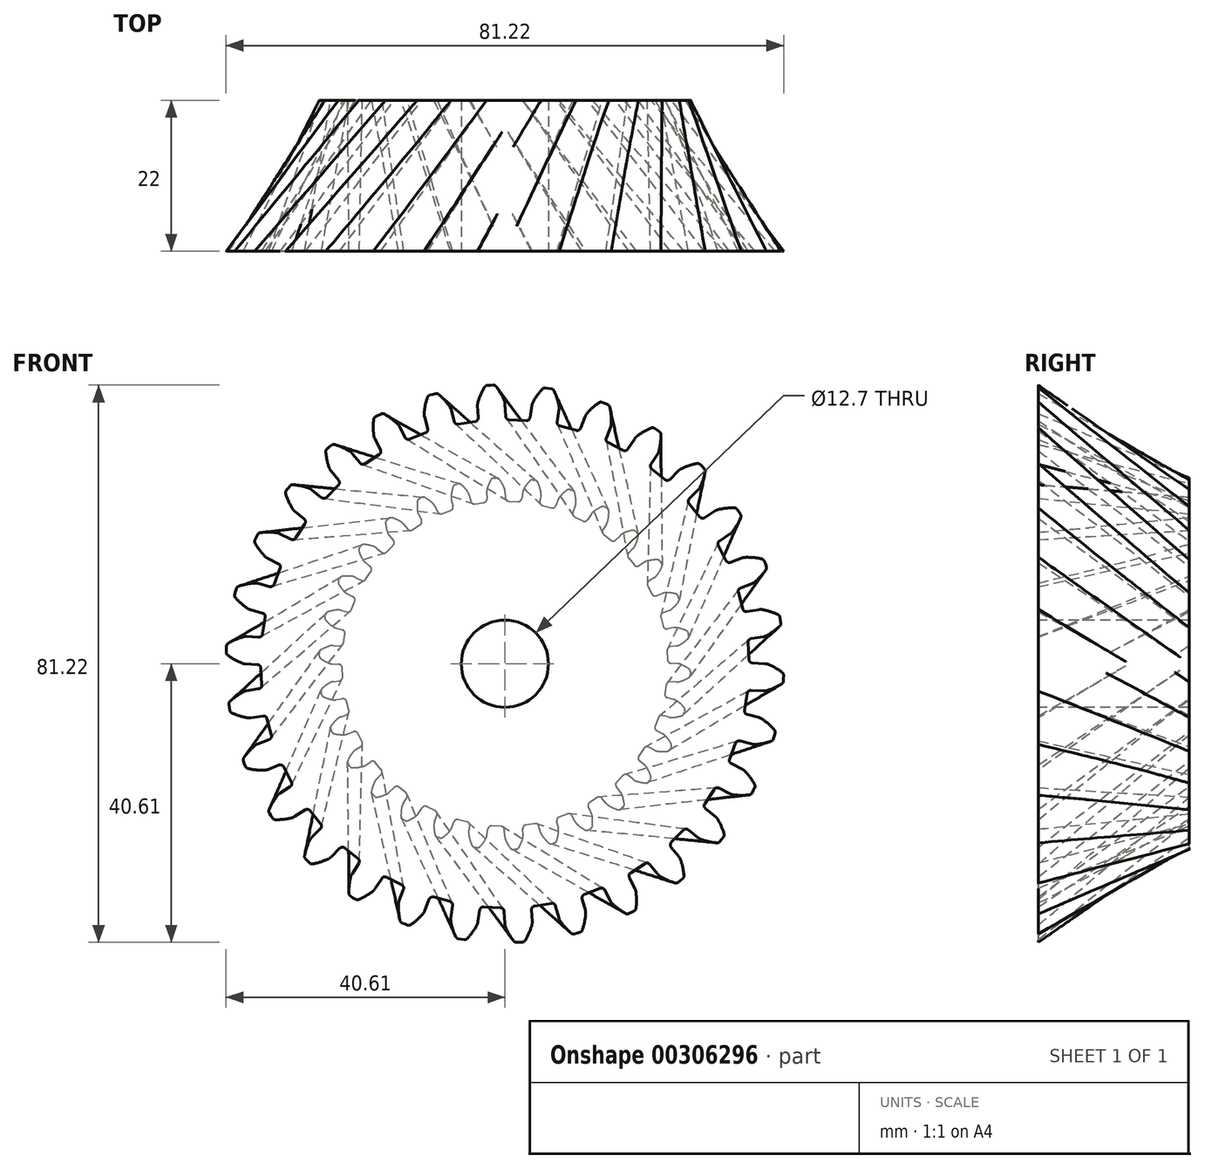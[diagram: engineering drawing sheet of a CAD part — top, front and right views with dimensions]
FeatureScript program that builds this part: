
annotation { "Feature Type Name" : "Feature", "Feature Type Description" : "" }
export const myFeature = defineFeature(function(context is Context, id is Id, definition is map)
    precondition{}
    {
        {
            var Q0;
            Q0=qCreatedBy(makeId("Front.planeOp"),FACE);
            var sketch = newSketch(context, id + "F0", { "sketchPlane" : qUnion([Q0])});
            skArc(sketch, "E0.trimOffspring", {"start": v(-0.11, 25.69) * mm, "mid": v(-0.42, 26.29) * mm, "end": v(-0.78, 26.85) * mm});
            skLineSegment(sketch, "E1", {"start": v(-1.22, 27.06) * mm, "end": v(-1.42, 27.05) * mm});
            skLineSegment(sketch, "E2.MirrorCS", {"start": v(-1.61, 27.04) * mm, "end": v(-1.42, 27.05) * mm});
            skArc(sketch, "E3.MirrorCS", {"start": v(-2.57, 25.56) * mm, "mid": v(-2.33, 26.19) * mm, "end": v(-2.03, 26.79) * mm});
            skLineSegment(sketch, "E4", {"start": v(0.02, 25.13) * mm, "end": v(0.07, 24.2) * mm});
            skLineSegment(sketch, "E5.MirrorCS", {"start": v(-2.65, 25) * mm, "end": v(-2.6, 24.06) * mm});
            skPoint(sketch, "E6.orphan", {"position": v(-2.54, 23.04) * mm});
            skPoint(sketch, "E7.orphan", {"position": v(0.12, 23.18) * mm});
            skPoint(sketch, "E8.visualSharp", {"position": v(-2.66, 25.26) * mm});
            skArc(sketch, "E8.filletArc", {"start": v(-2.57, 25.56) * mm, "mid": v(-2.64, 25.28) * mm, "end": v(-2.65, 25) * mm});
            skPoint(sketch, "E9.visualSharp", {"position": v(0, 25.4) * mm});
            skArc(sketch, "E9.filletArc", {"start": v(0.02, 25.13) * mm, "mid": v(-0.02, 25.42) * mm, "end": v(-0.11, 25.69) * mm});
            skPoint(sketch, "E10.visualSharp", {"position": v(-1.88, 27.03) * mm});
            skArc(sketch, "E10.filletArc", {"start": v(-1.61, 27.04) * mm, "mid": v(-1.85, 26.97) * mm, "end": v(-2.03, 26.79) * mm});
            skPoint(sketch, "E11.visualSharp", {"position": v(-0.95, 27.08) * mm});
            skArc(sketch, "E11.filletArc", {"start": v(-0.78, 26.85) * mm, "mid": v(-0.98, 27.01) * mm, "end": v(-1.22, 27.06) * mm});
            skPoint(sketch, "E12.visualSharp", {"position": v(-2.57, 23.57) * mm});
            skArc(sketch, "E12.filletArc", {"start": v(-3.06, 23.5) * mm, "mid": v(-2.72, 23.7) * mm, "end": v(-2.6, 24.06) * mm});
            skPoint(sketch, "E13.visualSharp", {"position": v(0.1, 23.7) * mm});
            skArc(sketch, "E13.filletArc", {"start": v(0.07, 24.2) * mm, "mid": v(0.23, 23.85) * mm, "end": v(0.59, 23.7) * mm});
            skLineSegment(sketch, "E14.1.0", {"start": v(-5.2, 24.58) * mm, "end": v(-4.97, 23.69) * mm});
            skPoint(sketch, "E14.1.1", {"position": v(-7.46, 26.05) * mm});
            skPoint(sketch, "E14.1.2", {"position": v(-6.56, 26.29) * mm});
            skPoint(sketch, "E14.1.3", {"position": v(-4.84, 23.2) * mm});
            skLineSegment(sketch, "E14.1.4", {"start": v(-7.78, 23.9) * mm, "end": v(-7.54, 23) * mm});
            skArc(sketch, "E14.1.5", {"start": v(-7.83, 24.47) * mm, "mid": v(-7.73, 25.13) * mm, "end": v(-7.55, 25.78) * mm});
            skPoint(sketch, "E14.1.6", {"position": v(-7.85, 24.16) * mm});
            skPoint(sketch, "E14.1.7", {"position": v(-7.42, 22.52) * mm});
            skArc(sketch, "E14.1.8", {"start": v(-5.45, 25.1) * mm, "mid": v(-5.87, 25.63) * mm, "end": v(-6.35, 26.1) * mm});
            skPoint(sketch, "E14.1.9", {"position": v(-5.28, 24.85) * mm});
            skPoint(sketch, "E14.1.10", {"position": v(-4.7, 22.7) * mm});
            skArc(sketch, "E14.1.11", {"start": v(-4.97, 23.69) * mm, "mid": v(-4.73, 23.38) * mm, "end": v(-4.35, 23.3) * mm});
            skArc(sketch, "E14.1.12", {"start": v(-7.83, 24.47) * mm, "mid": v(-7.83, 24.18) * mm, "end": v(-7.78, 23.9) * mm});
            skArc(sketch, "E14.1.13", {"start": v(-5.2, 24.58) * mm, "mid": v(-5.3, 24.86) * mm, "end": v(-5.45, 25.1) * mm});
            skArc(sketch, "E14.1.14", {"start": v(-7.88, 22.36) * mm, "mid": v(-7.59, 22.61) * mm, "end": v(-7.54, 23) * mm});
            skLineSegment(sketch, "E14.1.15", {"start": v(-6.82, 26.22) * mm, "end": v(-7.01, 26.17) * mm});
            skArc(sketch, "E14.1.16", {"start": v(-6.35, 26.1) * mm, "mid": v(-6.57, 26.22) * mm, "end": v(-6.82, 26.22) * mm});
            skLineSegment(sketch, "E14.1.17", {"start": v(-7.2, 26.12) * mm, "end": v(-7.01, 26.17) * mm});
            skArc(sketch, "E14.1.18", {"start": v(-7.2, 26.12) * mm, "mid": v(-7.42, 26) * mm, "end": v(-7.55, 25.78) * mm});
            skLineSegment(sketch, "E14.2.0", {"start": v(-10.2, 22.97) * mm, "end": v(-9.78, 22.14) * mm});
            skPoint(sketch, "E14.2.1", {"position": v(-12.71, 23.93) * mm});
            skPoint(sketch, "E14.2.2", {"position": v(-11.88, 24.35) * mm});
            skPoint(sketch, "E14.2.3", {"position": v(-9.56, 21.7) * mm});
            skLineSegment(sketch, "E14.2.4", {"start": v(-12.58, 21.75) * mm, "end": v(-12.16, 20.93) * mm});
            skArc(sketch, "E14.2.5", {"start": v(-12.75, 22.3) * mm, "mid": v(-12.78, 22.98) * mm, "end": v(-12.75, 23.65) * mm});
            skPoint(sketch, "E14.2.6", {"position": v(-12.7, 22) * mm});
            skPoint(sketch, "E14.2.7", {"position": v(-11.94, 20.48) * mm});
            skArc(sketch, "E14.2.8", {"start": v(-10.55, 23.42) * mm, "mid": v(-11.07, 23.85) * mm, "end": v(-11.64, 24.21) * mm});
            skPoint(sketch, "E14.2.9", {"position": v(-10.33, 23.2) * mm});
            skPoint(sketch, "E14.2.10", {"position": v(-9.32, 21.23) * mm});
            skArc(sketch, "E14.2.11", {"start": v(-9.78, 22.14) * mm, "mid": v(-9.5, 21.88) * mm, "end": v(-9.1, 21.89) * mm});
            skArc(sketch, "E14.2.12", {"start": v(-12.75, 22.3) * mm, "mid": v(-12.69, 22.02) * mm, "end": v(-12.58, 21.75) * mm});
            skArc(sketch, "E14.2.13", {"start": v(-10.2, 22.97) * mm, "mid": v(-10.36, 23.2) * mm, "end": v(-10.55, 23.42) * mm});
            skArc(sketch, "E14.2.14", {"start": v(-12.36, 20.23) * mm, "mid": v(-12.12, 20.54) * mm, "end": v(-12.16, 20.93) * mm});
            skLineSegment(sketch, "E14.2.15", {"start": v(-12.12, 24.23) * mm, "end": v(-12.3, 24.14) * mm});
            skArc(sketch, "E14.2.16", {"start": v(-11.64, 24.21) * mm, "mid": v(-11.88, 24.28) * mm, "end": v(-12.12, 24.23) * mm});
            skLineSegment(sketch, "E14.2.17", {"start": v(-12.47, 24.05) * mm, "end": v(-12.3, 24.14) * mm});
            skArc(sketch, "E14.2.18", {"start": v(-12.47, 24.05) * mm, "mid": v(-12.66, 23.88) * mm, "end": v(-12.75, 23.65) * mm});
            skPoint(sketch, "E14.center", {"position": v(0, 0) * mm});
            skPoint(sketch, "E15.3.3.0", {"position": v(-17.4, 20.76) * mm});
            skPoint(sketch, "E15.4.3.0", {"position": v(-16.69, 21.35) * mm});
            skPoint(sketch, "E15.5.3.0", {"position": v(-13.86, 19.23) * mm});
            skLineSegment(sketch, "E15.6.3.0", {"start": v(-16.83, 18.66) * mm, "end": v(-16.25, 17.94) * mm});
            skArc(sketch, "E15.9.3.0", {"start": v(-17.1, 19.17) * mm, "mid": v(-17.28, 19.82) * mm, "end": v(-17.39, 20.48) * mm});
            skPoint(sketch, "E15.13.3.0", {"position": v(-17, 18.87) * mm});
            skPoint(sketch, "E15.14.3.0", {"position": v(-15.93, 17.55) * mm});
            skArc(sketch, "E15.15.3.0", {"start": v(-15.2, 20.72) * mm, "mid": v(-15.8, 21.02) * mm, "end": v(-16.42, 21.26) * mm});
            skLineSegment(sketch, "E15.16.3.0", {"start": v(-14.75, 20.34) * mm, "end": v(-14.17, 19.62) * mm});
            skPoint(sketch, "E15.19.3.0", {"position": v(-14.93, 20.55) * mm});
            skPoint(sketch, "E15.20.3.0", {"position": v(-13.53, 18.82) * mm});
            skArc(sketch, "E15.21.3.0", {"start": v(-14.17, 19.62) * mm, "mid": v(-13.83, 19.43) * mm, "end": v(-13.45, 19.52) * mm});
            skArc(sketch, "E15.25.3.0", {"start": v(-17.1, 19.17) * mm, "mid": v(-17, 18.9) * mm, "end": v(-16.83, 18.66) * mm});
            skArc(sketch, "E15.29.3.0", {"start": v(-14.75, 20.34) * mm, "mid": v(-14.96, 20.55) * mm, "end": v(-15.2, 20.72) * mm});
            skArc(sketch, "E15.33.3.0", {"start": v(-16.3, 17.22) * mm, "mid": v(-16.13, 17.57) * mm, "end": v(-16.25, 17.94) * mm});
            skLineSegment(sketch, "E15.37.3.0", {"start": v(-16.9, 21.18) * mm, "end": v(-17.05, 21.05) * mm});
            skArc(sketch, "E15.40.3.0", {"start": v(-16.42, 21.26) * mm, "mid": v(-16.67, 21.28) * mm, "end": v(-16.9, 21.18) * mm});
            skLineSegment(sketch, "E15.44.3.0", {"start": v(-17.2, 20.93) * mm, "end": v(-17.05, 21.05) * mm});
            skArc(sketch, "E15.47.3.0", {"start": v(-17.2, 20.93) * mm, "mid": v(-17.35, 20.73) * mm, "end": v(-17.39, 20.48) * mm});
            skPoint(sketch, "E15.3.4.0", {"position": v(-21.35, 16.69) * mm});
            skPoint(sketch, "E15.4.4.0", {"position": v(-20.76, 17.4) * mm});
            skPoint(sketch, "E15.5.4.0", {"position": v(-17.55, 15.93) * mm});
            skLineSegment(sketch, "E15.6.4.0", {"start": v(-20.34, 14.75) * mm, "end": v(-19.62, 14.17) * mm});
            skArc(sketch, "E15.9.4.0", {"start": v(-20.72, 15.2) * mm, "mid": v(-21.02, 15.8) * mm, "end": v(-21.26, 16.42) * mm});
            skPoint(sketch, "E15.13.4.0", {"position": v(-20.55, 14.93) * mm});
            skPoint(sketch, "E15.14.4.0", {"position": v(-19.23, 13.86) * mm});
            skArc(sketch, "E15.15.4.0", {"start": v(-19.17, 17.1) * mm, "mid": v(-19.82, 17.28) * mm, "end": v(-20.48, 17.39) * mm});
            skLineSegment(sketch, "E15.16.4.0", {"start": v(-18.66, 16.83) * mm, "end": v(-17.94, 16.25) * mm});
            skPoint(sketch, "E15.19.4.0", {"position": v(-18.87, 17) * mm});
            skPoint(sketch, "E15.20.4.0", {"position": v(-17.14, 15.6) * mm});
            skArc(sketch, "E15.21.4.0", {"start": v(-17.94, 16.25) * mm, "mid": v(-17.57, 16.13) * mm, "end": v(-17.22, 16.3) * mm});
            skArc(sketch, "E15.25.4.0", {"start": v(-20.72, 15.2) * mm, "mid": v(-20.55, 14.96) * mm, "end": v(-20.34, 14.75) * mm});
            skArc(sketch, "E15.29.4.0", {"start": v(-18.66, 16.83) * mm, "mid": v(-18.9, 17) * mm, "end": v(-19.17, 17.1) * mm});
            skArc(sketch, "E15.33.4.0", {"start": v(-19.52, 13.45) * mm, "mid": v(-19.43, 13.83) * mm, "end": v(-19.62, 14.17) * mm});
            skLineSegment(sketch, "E15.37.4.0", {"start": v(-20.93, 17.2) * mm, "end": v(-21.05, 17.05) * mm});
            skArc(sketch, "E15.40.4.0", {"start": v(-20.48, 17.39) * mm, "mid": v(-20.73, 17.35) * mm, "end": v(-20.93, 17.2) * mm});
            skLineSegment(sketch, "E15.44.4.0", {"start": v(-21.18, 16.9) * mm, "end": v(-21.05, 17.05) * mm});
            skArc(sketch, "E15.47.4.0", {"start": v(-21.18, 16.9) * mm, "mid": v(-21.28, 16.67) * mm, "end": v(-21.26, 16.42) * mm});
            skPoint(sketch, "E15.3.5.0", {"position": v(-24.35, 11.88) * mm});
            skPoint(sketch, "E15.4.5.0", {"position": v(-23.93, 12.71) * mm});
            skPoint(sketch, "E15.5.5.0", {"position": v(-20.48, 11.94) * mm});
            skLineSegment(sketch, "E15.6.5.0", {"start": v(-22.97, 10.2) * mm, "end": v(-22.14, 9.78) * mm});
            skArc(sketch, "E15.9.5.0", {"start": v(-23.42, 10.55) * mm, "mid": v(-23.85, 11.07) * mm, "end": v(-24.21, 11.64) * mm});
            skPoint(sketch, "E15.13.5.0", {"position": v(-23.2, 10.33) * mm});
            skPoint(sketch, "E15.14.5.0", {"position": v(-21.7, 9.56) * mm});
            skArc(sketch, "E15.15.5.0", {"start": v(-22.3, 12.75) * mm, "mid": v(-22.98, 12.78) * mm, "end": v(-23.65, 12.75) * mm});
            skLineSegment(sketch, "E15.16.5.0", {"start": v(-21.75, 12.58) * mm, "end": v(-20.93, 12.16) * mm});
            skPoint(sketch, "E15.19.5.0", {"position": v(-22, 12.7) * mm});
            skPoint(sketch, "E15.20.5.0", {"position": v(-20.01, 11.7) * mm});
            skArc(sketch, "E15.21.5.0", {"start": v(-20.93, 12.16) * mm, "mid": v(-20.54, 12.12) * mm, "end": v(-20.23, 12.36) * mm});
            skArc(sketch, "E15.25.5.0", {"start": v(-23.42, 10.55) * mm, "mid": v(-23.2, 10.36) * mm, "end": v(-22.97, 10.2) * mm});
            skArc(sketch, "E15.29.5.0", {"start": v(-21.75, 12.58) * mm, "mid": v(-22.02, 12.69) * mm, "end": v(-22.3, 12.75) * mm});
            skArc(sketch, "E15.33.5.0", {"start": v(-21.89, 9.1) * mm, "mid": v(-21.88, 9.5) * mm, "end": v(-22.14, 9.78) * mm});
            skLineSegment(sketch, "E15.37.5.0", {"start": v(-24.05, 12.47) * mm, "end": v(-24.14, 12.3) * mm});
            skArc(sketch, "E15.40.5.0", {"start": v(-23.65, 12.75) * mm, "mid": v(-23.88, 12.66) * mm, "end": v(-24.05, 12.47) * mm});
            skLineSegment(sketch, "E15.44.5.0", {"start": v(-24.23, 12.12) * mm, "end": v(-24.14, 12.3) * mm});
            skArc(sketch, "E15.47.5.0", {"start": v(-24.23, 12.12) * mm, "mid": v(-24.28, 11.88) * mm, "end": v(-24.21, 11.64) * mm});
            skPoint(sketch, "E15.3.6.0", {"position": v(-26.29, 6.56) * mm});
            skPoint(sketch, "E15.4.6.0", {"position": v(-26.05, 7.46) * mm});
            skPoint(sketch, "E15.5.6.0", {"position": v(-22.52, 7.42) * mm});
            skLineSegment(sketch, "E15.6.6.0", {"start": v(-24.58, 5.2) * mm, "end": v(-23.69, 4.97) * mm});
            skArc(sketch, "E15.9.6.0", {"start": v(-25.1, 5.45) * mm, "mid": v(-25.63, 5.87) * mm, "end": v(-26.1, 6.35) * mm});
            skPoint(sketch, "E15.13.6.0", {"position": v(-24.85, 5.28) * mm});
            skPoint(sketch, "E15.14.6.0", {"position": v(-23.2, 4.84) * mm});
            skArc(sketch, "E15.15.6.0", {"start": v(-24.47, 7.83) * mm, "mid": v(-25.13, 7.73) * mm, "end": v(-25.78, 7.55) * mm});
            skLineSegment(sketch, "E15.16.6.0", {"start": v(-23.9, 7.78) * mm, "end": v(-23, 7.54) * mm});
            skPoint(sketch, "E15.19.6.0", {"position": v(-24.16, 7.85) * mm});
            skPoint(sketch, "E15.20.6.0", {"position": v(-22, 7.28) * mm});
            skArc(sketch, "E15.21.6.0", {"start": v(-23, 7.54) * mm, "mid": v(-22.61, 7.59) * mm, "end": v(-22.36, 7.88) * mm});
            skArc(sketch, "E15.25.6.0", {"start": v(-25.1, 5.45) * mm, "mid": v(-24.86, 5.3) * mm, "end": v(-24.58, 5.2) * mm});
            skArc(sketch, "E15.29.6.0", {"start": v(-23.9, 7.78) * mm, "mid": v(-24.18, 7.83) * mm, "end": v(-24.47, 7.83) * mm});
            skArc(sketch, "E15.33.6.0", {"start": v(-23.3, 4.35) * mm, "mid": v(-23.38, 4.73) * mm, "end": v(-23.69, 4.97) * mm});
            skLineSegment(sketch, "E15.37.6.0", {"start": v(-26.12, 7.2) * mm, "end": v(-26.17, 7.01) * mm});
            skArc(sketch, "E15.40.6.0", {"start": v(-25.78, 7.55) * mm, "mid": v(-26, 7.42) * mm, "end": v(-26.12, 7.2) * mm});
            skLineSegment(sketch, "E15.44.6.0", {"start": v(-26.22, 6.82) * mm, "end": v(-26.17, 7.01) * mm});
            skArc(sketch, "E15.47.6.0", {"start": v(-26.22, 6.82) * mm, "mid": v(-26.22, 6.57) * mm, "end": v(-26.1, 6.35) * mm});
            skPoint(sketch, "E15.3.7.0", {"position": v(-27.08, 0.95) * mm});
            skPoint(sketch, "E15.4.7.0", {"position": v(-27.03, 1.88) * mm});
            skPoint(sketch, "E15.5.7.0", {"position": v(-23.57, 2.57) * mm});
            skLineSegment(sketch, "E15.6.7.0", {"start": v(-25.13, -0.02) * mm, "end": v(-24.2, -0.07) * mm});
            skArc(sketch, "E15.9.7.0", {"start": v(-25.69, 0.11) * mm, "mid": v(-26.29, 0.42) * mm, "end": v(-26.85, 0.78) * mm});
            skPoint(sketch, "E15.13.7.0", {"position": v(-25.4, 0) * mm});
            skPoint(sketch, "E15.14.7.0", {"position": v(-23.7, -0.1) * mm});
            skArc(sketch, "E15.15.7.0", {"start": v(-25.56, 2.57) * mm, "mid": v(-26.19, 2.33) * mm, "end": v(-26.79, 2.03) * mm});
            skLineSegment(sketch, "E15.16.7.0", {"start": v(-25, 2.65) * mm, "end": v(-24.06, 2.6) * mm});
            skPoint(sketch, "E15.19.7.0", {"position": v(-25.26, 2.66) * mm});
            skPoint(sketch, "E15.20.7.0", {"position": v(-23.04, 2.54) * mm});
            skArc(sketch, "E15.21.7.0", {"start": v(-24.06, 2.6) * mm, "mid": v(-23.7, 2.72) * mm, "end": v(-23.5, 3.06) * mm});
            skArc(sketch, "E15.25.7.0", {"start": v(-25.69, 0.11) * mm, "mid": v(-25.42, 0.02) * mm, "end": v(-25.13, -0.02) * mm});
            skArc(sketch, "E15.29.7.0", {"start": v(-25, 2.65) * mm, "mid": v(-25.28, 2.64) * mm, "end": v(-25.56, 2.57) * mm});
            skArc(sketch, "E15.33.7.0", {"start": v(-23.7, -0.59) * mm, "mid": v(-23.85, -0.23) * mm, "end": v(-24.2, -0.07) * mm});
            skLineSegment(sketch, "E15.37.7.0", {"start": v(-27.04, 1.61) * mm, "end": v(-27.05, 1.42) * mm});
            skArc(sketch, "E15.40.7.0", {"start": v(-26.79, 2.03) * mm, "mid": v(-26.97, 1.85) * mm, "end": v(-27.04, 1.61) * mm});
            skLineSegment(sketch, "E15.44.7.0", {"start": v(-27.06, 1.22) * mm, "end": v(-27.05, 1.42) * mm});
            skArc(sketch, "E15.47.7.0", {"start": v(-27.06, 1.22) * mm, "mid": v(-27.01, 0.98) * mm, "end": v(-26.85, 0.78) * mm});
            skPoint(sketch, "E15.3.8.0", {"position": v(-26.68, -4.7) * mm});
            skPoint(sketch, "E15.4.8.0", {"position": v(-26.83, -3.78) * mm});
            skPoint(sketch, "E15.5.8.0", {"position": v(-23.59, -2.38) * mm});
            skLineSegment(sketch, "E15.6.8.0", {"start": v(-24.58, -5.24) * mm, "end": v(-23.66, -5.1) * mm});
            skArc(sketch, "E15.9.8.0", {"start": v(-25.15, -5.23) * mm, "mid": v(-25.8, -5.06) * mm, "end": v(-26.43, -4.82) * mm});
            skPoint(sketch, "E15.13.8.0", {"position": v(-24.84, -5.29) * mm});
            skPoint(sketch, "E15.14.8.0", {"position": v(-23.17, -5.02) * mm});
            skArc(sketch, "E15.15.8.0", {"start": v(-25.54, -2.8) * mm, "mid": v(-26.1, -3.16) * mm, "end": v(-26.62, -3.59) * mm});
            skLineSegment(sketch, "E15.16.8.0", {"start": v(-25, -2.6) * mm, "end": v(-24.08, -2.46) * mm});
            skPoint(sketch, "E15.19.8.0", {"position": v(-25.26, -2.65) * mm});
            skPoint(sketch, "E15.20.8.0", {"position": v(-23.07, -2.3) * mm});
            skArc(sketch, "E15.21.8.0", {"start": v(-24.08, -2.46) * mm, "mid": v(-23.74, -2.27) * mm, "end": v(-23.63, -1.9) * mm});
            skArc(sketch, "E15.25.8.0", {"start": v(-25.15, -5.23) * mm, "mid": v(-24.86, -5.26) * mm, "end": v(-24.58, -5.24) * mm});
            skArc(sketch, "E15.29.8.0", {"start": v(-25, -2.6) * mm, "mid": v(-25.27, -2.68) * mm, "end": v(-25.54, -2.8) * mm});
            skArc(sketch, "E15.33.8.0", {"start": v(-23.06, -5.5) * mm, "mid": v(-23.28, -5.18) * mm, "end": v(-23.66, -5.1) * mm});
            skLineSegment(sketch, "E15.37.8.0", {"start": v(-26.79, -4.04) * mm, "end": v(-26.76, -4.24) * mm});
            skArc(sketch, "E15.40.8.0", {"start": v(-26.62, -3.59) * mm, "mid": v(-26.76, -3.8) * mm, "end": v(-26.79, -4.04) * mm});
            skLineSegment(sketch, "E15.44.8.0", {"start": v(-26.73, -4.43) * mm, "end": v(-26.76, -4.24) * mm});
            skArc(sketch, "E15.47.8.0", {"start": v(-26.73, -4.43) * mm, "mid": v(-26.63, -4.66) * mm, "end": v(-26.43, -4.82) * mm});
            skPoint(sketch, "E15.3.9.0", {"position": v(-25.12, -10.14) * mm});
            skPoint(sketch, "E15.4.9.0", {"position": v(-25.46, -9.27) * mm});
            skPoint(sketch, "E15.5.9.0", {"position": v(-22.58, -7.24) * mm});
            skLineSegment(sketch, "E15.6.9.0", {"start": v(-22.95, -10.24) * mm, "end": v(-22.08, -9.9) * mm});
            skArc(sketch, "E15.9.9.0", {"start": v(-23.51, -10.34) * mm, "mid": v(-24.19, -10.31) * mm, "end": v(-24.85, -10.2) * mm});
            skPoint(sketch, "E15.13.9.0", {"position": v(-23.2, -10.34) * mm});
            skPoint(sketch, "E15.14.9.0", {"position": v(-21.62, -9.73) * mm});
            skArc(sketch, "E15.15.9.0", {"start": v(-24.4, -8.05) * mm, "mid": v(-24.87, -8.52) * mm, "end": v(-25.3, -9.04) * mm});
            skLineSegment(sketch, "E15.16.9.0", {"start": v(-23.9, -7.75) * mm, "end": v(-23.04, -7.41) * mm});
            skPoint(sketch, "E15.19.9.0", {"position": v(-24.16, -7.84) * mm});
            skPoint(sketch, "E15.20.9.0", {"position": v(-22.08, -7.05) * mm});
            skArc(sketch, "E15.21.9.0", {"start": v(-23.04, -7.41) * mm, "mid": v(-22.75, -7.15) * mm, "end": v(-22.72, -6.76) * mm});
            skArc(sketch, "E15.25.9.0", {"start": v(-23.51, -10.34) * mm, "mid": v(-23.23, -10.32) * mm, "end": v(-22.95, -10.24) * mm});
            skArc(sketch, "E15.29.9.0", {"start": v(-23.9, -7.75) * mm, "mid": v(-24.16, -7.87) * mm, "end": v(-24.4, -8.05) * mm});
            skArc(sketch, "E15.33.9.0", {"start": v(-21.41, -10.18) * mm, "mid": v(-21.7, -9.91) * mm, "end": v(-22.08, -9.9) * mm});
            skLineSegment(sketch, "E15.37.9.0", {"start": v(-25.36, -9.52) * mm, "end": v(-25.3, -9.7) * mm});
            skArc(sketch, "E15.40.9.0", {"start": v(-25.3, -9.04) * mm, "mid": v(-25.39, -9.28) * mm, "end": v(-25.36, -9.52) * mm});
            skLineSegment(sketch, "E15.44.9.0", {"start": v(-25.22, -9.9) * mm, "end": v(-25.3, -9.7) * mm});
            skArc(sketch, "E15.47.9.0", {"start": v(-25.22, -9.9) * mm, "mid": v(-25.08, -10.1) * mm, "end": v(-24.85, -10.2) * mm});
            skPoint(sketch, "E15.3.10.0", {"position": v(-22.47, -15.14) * mm});
            skPoint(sketch, "E15.4.10.0", {"position": v(-22.97, -14.36) * mm});
            skPoint(sketch, "E15.5.10.0", {"position": v(-20.58, -11.77) * mm});
            skLineSegment(sketch, "E15.6.10.0", {"start": v(-20.32, -14.79) * mm, "end": v(-19.54, -14.28) * mm});
            skArc(sketch, "E15.9.10.0", {"start": v(-20.85, -15) * mm, "mid": v(-21.51, -15.11) * mm, "end": v(-22.19, -15.15) * mm});
            skPoint(sketch, "E15.13.10.0", {"position": v(-20.55, -14.93) * mm});
            skPoint(sketch, "E15.14.10.0", {"position": v(-19.12, -14.01) * mm});
            skArc(sketch, "E15.15.10.0", {"start": v(-22.2, -12.94) * mm, "mid": v(-22.56, -13.5) * mm, "end": v(-22.86, -14.1) * mm});
            skLineSegment(sketch, "E15.16.10.0", {"start": v(-21.77, -12.55) * mm, "end": v(-21, -12.04) * mm});
            skPoint(sketch, "E15.19.10.0", {"position": v(-22, -12.7) * mm});
            skPoint(sketch, "E15.20.10.0", {"position": v(-20.14, -11.48) * mm});
            skArc(sketch, "E15.21.10.0", {"start": v(-21, -12.04) * mm, "mid": v(-20.77, -11.73) * mm, "end": v(-20.82, -11.34) * mm});
            skArc(sketch, "E15.25.10.0", {"start": v(-20.85, -15) * mm, "mid": v(-20.57, -14.92) * mm, "end": v(-20.32, -14.79) * mm});
            skArc(sketch, "E15.29.10.0", {"start": v(-21.77, -12.55) * mm, "mid": v(-22, -12.73) * mm, "end": v(-22.2, -12.94) * mm});
            skArc(sketch, "E15.33.10.0", {"start": v(-18.83, -14.4) * mm, "mid": v(-19.16, -14.2) * mm, "end": v(-19.54, -14.28) * mm});
            skLineSegment(sketch, "E15.37.10.0", {"start": v(-22.83, -14.59) * mm, "end": v(-22.72, -14.75) * mm});
            skArc(sketch, "E15.40.10.0", {"start": v(-22.86, -14.1) * mm, "mid": v(-22.9, -14.35) * mm, "end": v(-22.83, -14.59) * mm});
            skLineSegment(sketch, "E15.44.10.0", {"start": v(-22.61, -14.92) * mm, "end": v(-22.72, -14.75) * mm});
            skArc(sketch, "E15.47.10.0", {"start": v(-22.61, -14.92) * mm, "mid": v(-22.43, -15.09) * mm, "end": v(-22.19, -15.15) * mm});
            skPoint(sketch, "E15.3.11.0", {"position": v(-18.83, -19.48) * mm});
            skPoint(sketch, "E15.4.11.0", {"position": v(-19.48, -18.83) * mm});
            skPoint(sketch, "E15.5.11.0", {"position": v(-17.68, -15.8) * mm});
            skLineSegment(sketch, "E15.6.11.0", {"start": v(-16.8, -18.69) * mm, "end": v(-16.15, -18.03) * mm});
            skArc(sketch, "E15.9.11.0", {"start": v(-17.27, -19.01) * mm, "mid": v(-17.9, -19.26) * mm, "end": v(-18.55, -19.43) * mm});
            skPoint(sketch, "E15.13.11.0", {"position": v(-17, -18.88) * mm});
            skPoint(sketch, "E15.14.11.0", {"position": v(-15.8, -17.68) * mm});
            skArc(sketch, "E15.15.11.0", {"start": v(-19.01, -17.27) * mm, "mid": v(-19.26, -17.9) * mm, "end": v(-19.43, -18.55) * mm});
            skLineSegment(sketch, "E15.16.11.0", {"start": v(-18.69, -16.8) * mm, "end": v(-18.03, -16.15) * mm});
            skPoint(sketch, "E15.19.11.0", {"position": v(-18.88, -17) * mm});
            skPoint(sketch, "E15.20.11.0", {"position": v(-17.3, -15.42) * mm});
            skArc(sketch, "E15.21.11.0", {"start": v(-18.03, -16.15) * mm, "mid": v(-17.88, -15.79) * mm, "end": v(-18, -15.42) * mm});
            skArc(sketch, "E15.25.11.0", {"start": v(-17.27, -19.01) * mm, "mid": v(-17.02, -18.87) * mm, "end": v(-16.8, -18.69) * mm});
            skArc(sketch, "E15.29.11.0", {"start": v(-18.69, -16.8) * mm, "mid": v(-18.87, -17.02) * mm, "end": v(-19.01, -17.27) * mm});
            skArc(sketch, "E15.33.11.0", {"start": v(-15.42, -18) * mm, "mid": v(-15.79, -17.88) * mm, "end": v(-16.15, -18.03) * mm});
            skLineSegment(sketch, "E15.37.11.0", {"start": v(-19.3, -19.02) * mm, "end": v(-19.16, -19.16) * mm});
            skArc(sketch, "E15.40.11.0", {"start": v(-19.43, -18.55) * mm, "mid": v(-19.42, -18.8) * mm, "end": v(-19.3, -19.02) * mm});
            skLineSegment(sketch, "E15.44.11.0", {"start": v(-19.02, -19.3) * mm, "end": v(-19.16, -19.16) * mm});
            skArc(sketch, "E15.47.11.0", {"start": v(-19.02, -19.3) * mm, "mid": v(-18.8, -19.42) * mm, "end": v(-18.55, -19.43) * mm});
            skPoint(sketch, "E15.3.12.0", {"position": v(-14.36, -22.97) * mm});
            skPoint(sketch, "E15.4.12.0", {"position": v(-15.14, -22.47) * mm});
            skPoint(sketch, "E15.5.12.0", {"position": v(-14.01, -19.12) * mm});
            skLineSegment(sketch, "E15.6.12.0", {"start": v(-12.55, -21.77) * mm, "end": v(-12.04, -21) * mm});
            skArc(sketch, "E15.9.12.0", {"start": v(-12.94, -22.2) * mm, "mid": v(-13.5, -22.56) * mm, "end": v(-14.1, -22.86) * mm});
            skPoint(sketch, "E15.13.12.0", {"position": v(-12.7, -22) * mm});
            skPoint(sketch, "E15.14.12.0", {"position": v(-11.77, -20.58) * mm});
            skArc(sketch, "E15.15.12.0", {"start": v(-15, -20.85) * mm, "mid": v(-15.11, -21.51) * mm, "end": v(-15.15, -22.19) * mm});
            skLineSegment(sketch, "E15.16.12.0", {"start": v(-14.79, -20.32) * mm, "end": v(-14.28, -19.54) * mm});
            skPoint(sketch, "E15.19.12.0", {"position": v(-14.93, -20.55) * mm});
            skPoint(sketch, "E15.20.12.0", {"position": v(-13.72, -18.68) * mm});
            skArc(sketch, "E15.21.12.0", {"start": v(-14.28, -19.54) * mm, "mid": v(-14.2, -19.16) * mm, "end": v(-14.4, -18.83) * mm});
            skArc(sketch, "E15.25.12.0", {"start": v(-12.94, -22.2) * mm, "mid": v(-12.73, -22) * mm, "end": v(-12.55, -21.77) * mm});
            skArc(sketch, "E15.29.12.0", {"start": v(-14.79, -20.32) * mm, "mid": v(-14.92, -20.57) * mm, "end": v(-15, -20.85) * mm});
            skArc(sketch, "E15.33.12.0", {"start": v(-11.34, -20.82) * mm, "mid": v(-11.73, -20.77) * mm, "end": v(-12.04, -21) * mm});
            skLineSegment(sketch, "E15.37.12.0", {"start": v(-14.92, -22.61) * mm, "end": v(-14.75, -22.72) * mm});
            skArc(sketch, "E15.40.12.0", {"start": v(-15.15, -22.19) * mm, "mid": v(-15.09, -22.43) * mm, "end": v(-14.92, -22.61) * mm});
            skLineSegment(sketch, "E15.44.12.0", {"start": v(-14.59, -22.83) * mm, "end": v(-14.75, -22.72) * mm});
            skArc(sketch, "E15.47.12.0", {"start": v(-14.59, -22.83) * mm, "mid": v(-14.35, -22.9) * mm, "end": v(-14.1, -22.86) * mm});
            skPoint(sketch, "E15.3.13.0", {"position": v(-9.27, -25.46) * mm});
            skPoint(sketch, "E15.4.13.0", {"position": v(-10.14, -25.12) * mm});
            skPoint(sketch, "E15.5.13.0", {"position": v(-9.73, -21.62) * mm});
            skLineSegment(sketch, "E15.6.13.0", {"start": v(-7.75, -23.9) * mm, "end": v(-7.41, -23.04) * mm});
            skArc(sketch, "E15.9.13.0", {"start": v(-8.05, -24.4) * mm, "mid": v(-8.52, -24.87) * mm, "end": v(-9.04, -25.3) * mm});
            skPoint(sketch, "E15.13.13.0", {"position": v(-7.84, -24.16) * mm});
            skPoint(sketch, "E15.14.13.0", {"position": v(-7.24, -22.58) * mm});
            skArc(sketch, "E15.15.13.0", {"start": v(-10.34, -23.51) * mm, "mid": v(-10.31, -24.19) * mm, "end": v(-10.2, -24.85) * mm});
            skLineSegment(sketch, "E15.16.13.0", {"start": v(-10.24, -22.95) * mm, "end": v(-9.9, -22.08) * mm});
            skPoint(sketch, "E15.19.13.0", {"position": v(-10.34, -23.2) * mm});
            skPoint(sketch, "E15.20.13.0", {"position": v(-9.54, -21.13) * mm});
            skArc(sketch, "E15.21.13.0", {"start": v(-9.9, -22.08) * mm, "mid": v(-9.91, -21.7) * mm, "end": v(-10.18, -21.41) * mm});
            skArc(sketch, "E15.25.13.0", {"start": v(-8.05, -24.4) * mm, "mid": v(-7.87, -24.16) * mm, "end": v(-7.75, -23.9) * mm});
            skArc(sketch, "E15.29.13.0", {"start": v(-10.24, -22.95) * mm, "mid": v(-10.32, -23.23) * mm, "end": v(-10.34, -23.51) * mm});
            skArc(sketch, "E15.33.13.0", {"start": v(-6.76, -22.72) * mm, "mid": v(-7.15, -22.75) * mm, "end": v(-7.41, -23.04) * mm});
            skLineSegment(sketch, "E15.37.13.0", {"start": v(-9.9, -25.22) * mm, "end": v(-9.7, -25.3) * mm});
            skArc(sketch, "E15.40.13.0", {"start": v(-10.2, -24.85) * mm, "mid": v(-10.1, -25.08) * mm, "end": v(-9.9, -25.22) * mm});
            skLineSegment(sketch, "E15.44.13.0", {"start": v(-9.52, -25.36) * mm, "end": v(-9.7, -25.3) * mm});
            skArc(sketch, "E15.47.13.0", {"start": v(-9.52, -25.36) * mm, "mid": v(-9.28, -25.39) * mm, "end": v(-9.04, -25.3) * mm});
            skPoint(sketch, "E15.3.14.0", {"position": v(-3.78, -26.83) * mm});
            skPoint(sketch, "E15.4.14.0", {"position": v(-4.7, -26.68) * mm});
            skPoint(sketch, "E15.5.14.0", {"position": v(-5.02, -23.17) * mm});
            skLineSegment(sketch, "E15.6.14.0", {"start": v(-2.6, -25) * mm, "end": v(-2.46, -24.08) * mm});
            skArc(sketch, "E15.9.14.0", {"start": v(-2.8, -25.54) * mm, "mid": v(-3.16, -26.1) * mm, "end": v(-3.59, -26.62) * mm});
            skPoint(sketch, "E15.13.14.0", {"position": v(-2.65, -25.26) * mm});
            skPoint(sketch, "E15.14.14.0", {"position": v(-2.38, -23.59) * mm});
            skArc(sketch, "E15.15.14.0", {"start": v(-5.23, -25.15) * mm, "mid": v(-5.06, -25.8) * mm, "end": v(-4.82, -26.43) * mm});
            skLineSegment(sketch, "E15.16.14.0", {"start": v(-5.24, -24.58) * mm, "end": v(-5.1, -23.66) * mm});
            skPoint(sketch, "E15.19.14.0", {"position": v(-5.29, -24.84) * mm});
            skPoint(sketch, "E15.20.14.0", {"position": v(-4.94, -22.65) * mm});
            skArc(sketch, "E15.21.14.0", {"start": v(-5.1, -23.66) * mm, "mid": v(-5.18, -23.28) * mm, "end": v(-5.5, -23.06) * mm});
            skArc(sketch, "E15.25.14.0", {"start": v(-2.8, -25.54) * mm, "mid": v(-2.68, -25.27) * mm, "end": v(-2.6, -25) * mm});
            skArc(sketch, "E15.29.14.0", {"start": v(-5.24, -24.58) * mm, "mid": v(-5.26, -24.86) * mm, "end": v(-5.23, -25.15) * mm});
            skArc(sketch, "E15.33.14.0", {"start": v(-1.9, -23.63) * mm, "mid": v(-2.27, -23.74) * mm, "end": v(-2.46, -24.08) * mm});
            skLineSegment(sketch, "E15.37.14.0", {"start": v(-4.43, -26.73) * mm, "end": v(-4.24, -26.76) * mm});
            skArc(sketch, "E15.40.14.0", {"start": v(-4.82, -26.43) * mm, "mid": v(-4.66, -26.63) * mm, "end": v(-4.43, -26.73) * mm});
            skLineSegment(sketch, "E15.44.14.0", {"start": v(-4.04, -26.79) * mm, "end": v(-4.24, -26.76) * mm});
            skArc(sketch, "E15.47.14.0", {"start": v(-4.04, -26.79) * mm, "mid": v(-3.8, -26.76) * mm, "end": v(-3.59, -26.62) * mm});
            skPoint(sketch, "E15.3.15.0", {"position": v(1.88, -27.03) * mm});
            skPoint(sketch, "E15.4.15.0", {"position": v(0.95, -27.08) * mm});
            skPoint(sketch, "E15.5.15.0", {"position": v(-0.1, -23.7) * mm});
            skLineSegment(sketch, "E15.6.15.0", {"start": v(2.65, -25) * mm, "end": v(2.6, -24.06) * mm});
            skArc(sketch, "E15.9.15.0", {"start": v(2.57, -25.56) * mm, "mid": v(2.33, -26.19) * mm, "end": v(2.03, -26.79) * mm});
            skPoint(sketch, "E15.13.15.0", {"position": v(2.66, -25.26) * mm});
            skPoint(sketch, "E15.14.15.0", {"position": v(2.57, -23.57) * mm});
            skArc(sketch, "E15.15.15.0", {"start": v(0.11, -25.69) * mm, "mid": v(0.42, -26.29) * mm, "end": v(0.78, -26.85) * mm});
            skLineSegment(sketch, "E15.16.15.0", {"start": v(-0.02, -25.13) * mm, "end": v(-0.07, -24.2) * mm});
            skPoint(sketch, "E15.19.15.0", {"position": v(0, -25.4) * mm});
            skPoint(sketch, "E15.20.15.0", {"position": v(-0.12, -23.18) * mm});
            skArc(sketch, "E15.21.15.0", {"start": v(-0.07, -24.2) * mm, "mid": v(-0.23, -23.85) * mm, "end": v(-0.59, -23.7) * mm});
            skArc(sketch, "E15.25.15.0", {"start": v(2.57, -25.56) * mm, "mid": v(2.64, -25.28) * mm, "end": v(2.65, -25) * mm});
            skArc(sketch, "E15.29.15.0", {"start": v(-0.02, -25.13) * mm, "mid": v(0.02, -25.42) * mm, "end": v(0.11, -25.69) * mm});
            skArc(sketch, "E15.33.15.0", {"start": v(3.06, -23.5) * mm, "mid": v(2.72, -23.7) * mm, "end": v(2.6, -24.06) * mm});
            skLineSegment(sketch, "E15.37.15.0", {"start": v(1.22, -27.06) * mm, "end": v(1.42, -27.05) * mm});
            skArc(sketch, "E15.40.15.0", {"start": v(0.78, -26.85) * mm, "mid": v(0.98, -27.01) * mm, "end": v(1.22, -27.06) * mm});
            skLineSegment(sketch, "E15.44.15.0", {"start": v(1.61, -27.04) * mm, "end": v(1.42, -27.05) * mm});
            skArc(sketch, "E15.47.15.0", {"start": v(1.61, -27.04) * mm, "mid": v(1.85, -26.97) * mm, "end": v(2.03, -26.79) * mm});
            skPoint(sketch, "E15.3.16.0", {"position": v(7.46, -26.05) * mm});
            skPoint(sketch, "E15.4.16.0", {"position": v(6.56, -26.29) * mm});
            skPoint(sketch, "E15.5.16.0", {"position": v(4.84, -23.2) * mm});
            skLineSegment(sketch, "E15.6.16.0", {"start": v(7.78, -23.9) * mm, "end": v(7.54, -23) * mm});
            skArc(sketch, "E15.9.16.0", {"start": v(7.83, -24.47) * mm, "mid": v(7.73, -25.13) * mm, "end": v(7.55, -25.78) * mm});
            skPoint(sketch, "E15.13.16.0", {"position": v(7.85, -24.16) * mm});
            skPoint(sketch, "E15.14.16.0", {"position": v(7.42, -22.52) * mm});
            skArc(sketch, "E15.15.16.0", {"start": v(5.45, -25.1) * mm, "mid": v(5.87, -25.63) * mm, "end": v(6.35, -26.1) * mm});
            skLineSegment(sketch, "E15.16.16.0", {"start": v(5.2, -24.58) * mm, "end": v(4.97, -23.69) * mm});
            skPoint(sketch, "E15.19.16.0", {"position": v(5.28, -24.85) * mm});
            skPoint(sketch, "E15.20.16.0", {"position": v(4.7, -22.7) * mm});
            skArc(sketch, "E15.21.16.0", {"start": v(4.97, -23.69) * mm, "mid": v(4.73, -23.38) * mm, "end": v(4.35, -23.3) * mm});
            skArc(sketch, "E15.25.16.0", {"start": v(7.83, -24.47) * mm, "mid": v(7.83, -24.18) * mm, "end": v(7.78, -23.9) * mm});
            skArc(sketch, "E15.29.16.0", {"start": v(5.2, -24.58) * mm, "mid": v(5.3, -24.86) * mm, "end": v(5.45, -25.1) * mm});
            skArc(sketch, "E15.33.16.0", {"start": v(7.88, -22.36) * mm, "mid": v(7.59, -22.61) * mm, "end": v(7.54, -23) * mm});
            skLineSegment(sketch, "E15.37.16.0", {"start": v(6.82, -26.22) * mm, "end": v(7.01, -26.17) * mm});
            skArc(sketch, "E15.40.16.0", {"start": v(6.35, -26.1) * mm, "mid": v(6.57, -26.22) * mm, "end": v(6.82, -26.22) * mm});
            skLineSegment(sketch, "E15.44.16.0", {"start": v(7.2, -26.12) * mm, "end": v(7.01, -26.17) * mm});
            skArc(sketch, "E15.47.16.0", {"start": v(7.2, -26.12) * mm, "mid": v(7.42, -26) * mm, "end": v(7.55, -25.78) * mm});
            skPoint(sketch, "E15.3.17.0", {"position": v(12.71, -23.93) * mm});
            skPoint(sketch, "E15.4.17.0", {"position": v(11.88, -24.35) * mm});
            skPoint(sketch, "E15.5.17.0", {"position": v(9.56, -21.7) * mm});
            skLineSegment(sketch, "E15.6.17.0", {"start": v(12.58, -21.75) * mm, "end": v(12.16, -20.93) * mm});
            skArc(sketch, "E15.9.17.0", {"start": v(12.75, -22.3) * mm, "mid": v(12.78, -22.98) * mm, "end": v(12.75, -23.65) * mm});
            skPoint(sketch, "E15.13.17.0", {"position": v(12.7, -22) * mm});
            skPoint(sketch, "E15.14.17.0", {"position": v(11.94, -20.48) * mm});
            skArc(sketch, "E15.15.17.0", {"start": v(10.55, -23.42) * mm, "mid": v(11.07, -23.85) * mm, "end": v(11.64, -24.21) * mm});
            skLineSegment(sketch, "E15.16.17.0", {"start": v(10.2, -22.97) * mm, "end": v(9.78, -22.14) * mm});
            skPoint(sketch, "E15.19.17.0", {"position": v(10.33, -23.2) * mm});
            skPoint(sketch, "E15.20.17.0", {"position": v(9.32, -21.23) * mm});
            skArc(sketch, "E15.21.17.0", {"start": v(9.78, -22.14) * mm, "mid": v(9.5, -21.88) * mm, "end": v(9.1, -21.89) * mm});
            skArc(sketch, "E15.25.17.0", {"start": v(12.75, -22.3) * mm, "mid": v(12.69, -22.02) * mm, "end": v(12.58, -21.75) * mm});
            skArc(sketch, "E15.29.17.0", {"start": v(10.2, -22.97) * mm, "mid": v(10.36, -23.2) * mm, "end": v(10.55, -23.42) * mm});
            skArc(sketch, "E15.33.17.0", {"start": v(12.36, -20.23) * mm, "mid": v(12.12, -20.54) * mm, "end": v(12.16, -20.93) * mm});
            skLineSegment(sketch, "E15.37.17.0", {"start": v(12.12, -24.23) * mm, "end": v(12.3, -24.14) * mm});
            skArc(sketch, "E15.40.17.0", {"start": v(11.64, -24.21) * mm, "mid": v(11.88, -24.28) * mm, "end": v(12.12, -24.23) * mm});
            skLineSegment(sketch, "E15.44.17.0", {"start": v(12.47, -24.05) * mm, "end": v(12.3, -24.14) * mm});
            skArc(sketch, "E15.47.17.0", {"start": v(12.47, -24.05) * mm, "mid": v(12.66, -23.88) * mm, "end": v(12.75, -23.65) * mm});
            skPoint(sketch, "E15.3.18.0", {"position": v(17.4, -20.76) * mm});
            skPoint(sketch, "E15.4.18.0", {"position": v(16.69, -21.35) * mm});
            skPoint(sketch, "E15.5.18.0", {"position": v(13.86, -19.23) * mm});
            skLineSegment(sketch, "E15.6.18.0", {"start": v(16.83, -18.66) * mm, "end": v(16.25, -17.94) * mm});
            skArc(sketch, "E15.9.18.0", {"start": v(17.1, -19.17) * mm, "mid": v(17.28, -19.82) * mm, "end": v(17.39, -20.48) * mm});
            skPoint(sketch, "E15.13.18.0", {"position": v(17, -18.87) * mm});
            skPoint(sketch, "E15.14.18.0", {"position": v(15.93, -17.55) * mm});
            skArc(sketch, "E15.15.18.0", {"start": v(15.2, -20.72) * mm, "mid": v(15.8, -21.02) * mm, "end": v(16.42, -21.26) * mm});
            skLineSegment(sketch, "E15.16.18.0", {"start": v(14.75, -20.34) * mm, "end": v(14.17, -19.62) * mm});
            skPoint(sketch, "E15.19.18.0", {"position": v(14.93, -20.55) * mm});
            skPoint(sketch, "E15.20.18.0", {"position": v(13.53, -18.82) * mm});
            skArc(sketch, "E15.21.18.0", {"start": v(14.17, -19.62) * mm, "mid": v(13.83, -19.43) * mm, "end": v(13.45, -19.52) * mm});
            skArc(sketch, "E15.25.18.0", {"start": v(17.1, -19.17) * mm, "mid": v(17, -18.9) * mm, "end": v(16.83, -18.66) * mm});
            skArc(sketch, "E15.29.18.0", {"start": v(14.75, -20.34) * mm, "mid": v(14.96, -20.55) * mm, "end": v(15.2, -20.72) * mm});
            skArc(sketch, "E15.33.18.0", {"start": v(16.3, -17.22) * mm, "mid": v(16.13, -17.57) * mm, "end": v(16.25, -17.94) * mm});
            skLineSegment(sketch, "E15.37.18.0", {"start": v(16.9, -21.18) * mm, "end": v(17.05, -21.05) * mm});
            skArc(sketch, "E15.40.18.0", {"start": v(16.42, -21.26) * mm, "mid": v(16.67, -21.28) * mm, "end": v(16.9, -21.18) * mm});
            skLineSegment(sketch, "E15.44.18.0", {"start": v(17.2, -20.93) * mm, "end": v(17.05, -21.05) * mm});
            skArc(sketch, "E15.47.18.0", {"start": v(17.2, -20.93) * mm, "mid": v(17.35, -20.73) * mm, "end": v(17.39, -20.48) * mm});
            skPoint(sketch, "E15.3.19.0", {"position": v(21.35, -16.69) * mm});
            skPoint(sketch, "E15.4.19.0", {"position": v(20.76, -17.4) * mm});
            skPoint(sketch, "E15.5.19.0", {"position": v(17.55, -15.93) * mm});
            skLineSegment(sketch, "E15.6.19.0", {"start": v(20.34, -14.75) * mm, "end": v(19.62, -14.17) * mm});
            skArc(sketch, "E15.9.19.0", {"start": v(20.72, -15.2) * mm, "mid": v(21.02, -15.8) * mm, "end": v(21.26, -16.42) * mm});
            skPoint(sketch, "E15.13.19.0", {"position": v(20.55, -14.93) * mm});
            skPoint(sketch, "E15.14.19.0", {"position": v(19.23, -13.86) * mm});
            skArc(sketch, "E15.15.19.0", {"start": v(19.17, -17.1) * mm, "mid": v(19.82, -17.28) * mm, "end": v(20.48, -17.39) * mm});
            skLineSegment(sketch, "E15.16.19.0", {"start": v(18.66, -16.83) * mm, "end": v(17.94, -16.25) * mm});
            skPoint(sketch, "E15.19.19.0", {"position": v(18.87, -17) * mm});
            skPoint(sketch, "E15.20.19.0", {"position": v(17.14, -15.6) * mm});
            skArc(sketch, "E15.21.19.0", {"start": v(17.94, -16.25) * mm, "mid": v(17.57, -16.13) * mm, "end": v(17.22, -16.3) * mm});
            skArc(sketch, "E15.25.19.0", {"start": v(20.72, -15.2) * mm, "mid": v(20.55, -14.96) * mm, "end": v(20.34, -14.75) * mm});
            skArc(sketch, "E15.29.19.0", {"start": v(18.66, -16.83) * mm, "mid": v(18.9, -17) * mm, "end": v(19.17, -17.1) * mm});
            skArc(sketch, "E15.33.19.0", {"start": v(19.52, -13.45) * mm, "mid": v(19.43, -13.83) * mm, "end": v(19.62, -14.17) * mm});
            skLineSegment(sketch, "E15.37.19.0", {"start": v(20.93, -17.2) * mm, "end": v(21.05, -17.05) * mm});
            skArc(sketch, "E15.40.19.0", {"start": v(20.48, -17.39) * mm, "mid": v(20.73, -17.35) * mm, "end": v(20.93, -17.2) * mm});
            skLineSegment(sketch, "E15.44.19.0", {"start": v(21.18, -16.9) * mm, "end": v(21.05, -17.05) * mm});
            skArc(sketch, "E15.47.19.0", {"start": v(21.18, -16.9) * mm, "mid": v(21.28, -16.67) * mm, "end": v(21.26, -16.42) * mm});
            skPoint(sketch, "E15.3.20.0", {"position": v(24.35, -11.88) * mm});
            skPoint(sketch, "E15.4.20.0", {"position": v(23.93, -12.71) * mm});
            skPoint(sketch, "E15.5.20.0", {"position": v(20.48, -11.94) * mm});
            skLineSegment(sketch, "E15.6.20.0", {"start": v(22.97, -10.2) * mm, "end": v(22.14, -9.78) * mm});
            skArc(sketch, "E15.9.20.0", {"start": v(23.42, -10.55) * mm, "mid": v(23.85, -11.07) * mm, "end": v(24.21, -11.64) * mm});
            skPoint(sketch, "E15.13.20.0", {"position": v(23.2, -10.33) * mm});
            skPoint(sketch, "E15.14.20.0", {"position": v(21.7, -9.56) * mm});
            skArc(sketch, "E15.15.20.0", {"start": v(22.3, -12.75) * mm, "mid": v(22.98, -12.78) * mm, "end": v(23.65, -12.75) * mm});
            skLineSegment(sketch, "E15.16.20.0", {"start": v(21.75, -12.58) * mm, "end": v(20.93, -12.16) * mm});
            skPoint(sketch, "E15.19.20.0", {"position": v(22, -12.7) * mm});
            skPoint(sketch, "E15.20.20.0", {"position": v(20.01, -11.7) * mm});
            skArc(sketch, "E15.21.20.0", {"start": v(20.93, -12.16) * mm, "mid": v(20.54, -12.12) * mm, "end": v(20.23, -12.36) * mm});
            skArc(sketch, "E15.25.20.0", {"start": v(23.42, -10.55) * mm, "mid": v(23.2, -10.36) * mm, "end": v(22.97, -10.2) * mm});
            skArc(sketch, "E15.29.20.0", {"start": v(21.75, -12.58) * mm, "mid": v(22.02, -12.69) * mm, "end": v(22.3, -12.75) * mm});
            skArc(sketch, "E15.33.20.0", {"start": v(21.89, -9.1) * mm, "mid": v(21.88, -9.5) * mm, "end": v(22.14, -9.78) * mm});
            skLineSegment(sketch, "E15.37.20.0", {"start": v(24.05, -12.47) * mm, "end": v(24.14, -12.3) * mm});
            skArc(sketch, "E15.40.20.0", {"start": v(23.65, -12.75) * mm, "mid": v(23.88, -12.66) * mm, "end": v(24.05, -12.47) * mm});
            skLineSegment(sketch, "E15.44.20.0", {"start": v(24.23, -12.12) * mm, "end": v(24.14, -12.3) * mm});
            skArc(sketch, "E15.47.20.0", {"start": v(24.23, -12.12) * mm, "mid": v(24.28, -11.88) * mm, "end": v(24.21, -11.64) * mm});
            skPoint(sketch, "E15.3.21.0", {"position": v(26.29, -6.56) * mm});
            skPoint(sketch, "E15.4.21.0", {"position": v(26.05, -7.46) * mm});
            skPoint(sketch, "E15.5.21.0", {"position": v(22.52, -7.42) * mm});
            skLineSegment(sketch, "E15.6.21.0", {"start": v(24.58, -5.2) * mm, "end": v(23.69, -4.97) * mm});
            skArc(sketch, "E15.9.21.0", {"start": v(25.1, -5.45) * mm, "mid": v(25.63, -5.87) * mm, "end": v(26.1, -6.35) * mm});
            skPoint(sketch, "E15.13.21.0", {"position": v(24.85, -5.28) * mm});
            skPoint(sketch, "E15.14.21.0", {"position": v(23.2, -4.84) * mm});
            skArc(sketch, "E15.15.21.0", {"start": v(24.47, -7.83) * mm, "mid": v(25.13, -7.73) * mm, "end": v(25.78, -7.55) * mm});
            skLineSegment(sketch, "E15.16.21.0", {"start": v(23.9, -7.78) * mm, "end": v(23, -7.54) * mm});
            skPoint(sketch, "E15.19.21.0", {"position": v(24.16, -7.85) * mm});
            skPoint(sketch, "E15.20.21.0", {"position": v(22, -7.28) * mm});
            skArc(sketch, "E15.21.21.0", {"start": v(23, -7.54) * mm, "mid": v(22.61, -7.59) * mm, "end": v(22.36, -7.88) * mm});
            skArc(sketch, "E15.25.21.0", {"start": v(25.1, -5.45) * mm, "mid": v(24.86, -5.3) * mm, "end": v(24.58, -5.2) * mm});
            skArc(sketch, "E15.29.21.0", {"start": v(23.9, -7.78) * mm, "mid": v(24.18, -7.83) * mm, "end": v(24.47, -7.83) * mm});
            skArc(sketch, "E15.33.21.0", {"start": v(23.3, -4.35) * mm, "mid": v(23.38, -4.73) * mm, "end": v(23.69, -4.97) * mm});
            skLineSegment(sketch, "E15.37.21.0", {"start": v(26.12, -7.2) * mm, "end": v(26.17, -7.01) * mm});
            skArc(sketch, "E15.40.21.0", {"start": v(25.78, -7.55) * mm, "mid": v(26, -7.42) * mm, "end": v(26.12, -7.2) * mm});
            skLineSegment(sketch, "E15.44.21.0", {"start": v(26.22, -6.82) * mm, "end": v(26.17, -7.01) * mm});
            skArc(sketch, "E15.47.21.0", {"start": v(26.22, -6.82) * mm, "mid": v(26.22, -6.57) * mm, "end": v(26.1, -6.35) * mm});
            skPoint(sketch, "E15.3.22.0", {"position": v(27.08, -0.95) * mm});
            skPoint(sketch, "E15.4.22.0", {"position": v(27.03, -1.88) * mm});
            skPoint(sketch, "E15.5.22.0", {"position": v(23.57, -2.57) * mm});
            skLineSegment(sketch, "E15.6.22.0", {"start": v(25.13, 0.02) * mm, "end": v(24.2, 0.07) * mm});
            skArc(sketch, "E15.9.22.0", {"start": v(25.69, -0.11) * mm, "mid": v(26.29, -0.42) * mm, "end": v(26.85, -0.78) * mm});
            skPoint(sketch, "E15.13.22.0", {"position": v(25.4, 0) * mm});
            skPoint(sketch, "E15.14.22.0", {"position": v(23.7, 0.1) * mm});
            skArc(sketch, "E15.15.22.0", {"start": v(25.56, -2.57) * mm, "mid": v(26.19, -2.33) * mm, "end": v(26.79, -2.03) * mm});
            skLineSegment(sketch, "E15.16.22.0", {"start": v(25, -2.65) * mm, "end": v(24.06, -2.6) * mm});
            skPoint(sketch, "E15.19.22.0", {"position": v(25.26, -2.66) * mm});
            skPoint(sketch, "E15.20.22.0", {"position": v(23.04, -2.54) * mm});
            skArc(sketch, "E15.21.22.0", {"start": v(24.06, -2.6) * mm, "mid": v(23.7, -2.72) * mm, "end": v(23.5, -3.06) * mm});
            skArc(sketch, "E15.25.22.0", {"start": v(25.69, -0.11) * mm, "mid": v(25.42, -0.02) * mm, "end": v(25.13, 0.02) * mm});
            skArc(sketch, "E15.29.22.0", {"start": v(25, -2.65) * mm, "mid": v(25.28, -2.64) * mm, "end": v(25.56, -2.57) * mm});
            skArc(sketch, "E15.33.22.0", {"start": v(23.7, 0.59) * mm, "mid": v(23.85, 0.23) * mm, "end": v(24.2, 0.07) * mm});
            skLineSegment(sketch, "E15.37.22.0", {"start": v(27.04, -1.61) * mm, "end": v(27.05, -1.42) * mm});
            skArc(sketch, "E15.40.22.0", {"start": v(26.79, -2.03) * mm, "mid": v(26.97, -1.85) * mm, "end": v(27.04, -1.61) * mm});
            skLineSegment(sketch, "E15.44.22.0", {"start": v(27.06, -1.22) * mm, "end": v(27.05, -1.42) * mm});
            skArc(sketch, "E15.47.22.0", {"start": v(27.06, -1.22) * mm, "mid": v(27.01, -0.98) * mm, "end": v(26.85, -0.78) * mm});
            skPoint(sketch, "E15.3.23.0", {"position": v(26.68, 4.7) * mm});
            skPoint(sketch, "E15.4.23.0", {"position": v(26.83, 3.78) * mm});
            skPoint(sketch, "E15.5.23.0", {"position": v(23.59, 2.38) * mm});
            skLineSegment(sketch, "E15.6.23.0", {"start": v(24.58, 5.24) * mm, "end": v(23.66, 5.1) * mm});
            skArc(sketch, "E15.9.23.0", {"start": v(25.15, 5.23) * mm, "mid": v(25.8, 5.06) * mm, "end": v(26.43, 4.82) * mm});
            skPoint(sketch, "E15.13.23.0", {"position": v(24.84, 5.29) * mm});
            skPoint(sketch, "E15.14.23.0", {"position": v(23.17, 5.02) * mm});
            skArc(sketch, "E15.15.23.0", {"start": v(25.54, 2.8) * mm, "mid": v(26.1, 3.16) * mm, "end": v(26.62, 3.59) * mm});
            skLineSegment(sketch, "E15.16.23.0", {"start": v(25, 2.6) * mm, "end": v(24.08, 2.46) * mm});
            skPoint(sketch, "E15.19.23.0", {"position": v(25.26, 2.65) * mm});
            skPoint(sketch, "E15.20.23.0", {"position": v(23.07, 2.3) * mm});
            skArc(sketch, "E15.21.23.0", {"start": v(24.08, 2.46) * mm, "mid": v(23.74, 2.27) * mm, "end": v(23.63, 1.9) * mm});
            skArc(sketch, "E15.25.23.0", {"start": v(25.15, 5.23) * mm, "mid": v(24.86, 5.26) * mm, "end": v(24.58, 5.24) * mm});
            skArc(sketch, "E15.29.23.0", {"start": v(25, 2.6) * mm, "mid": v(25.27, 2.68) * mm, "end": v(25.54, 2.8) * mm});
            skArc(sketch, "E15.33.23.0", {"start": v(23.06, 5.5) * mm, "mid": v(23.28, 5.18) * mm, "end": v(23.66, 5.1) * mm});
            skLineSegment(sketch, "E15.37.23.0", {"start": v(26.79, 4.04) * mm, "end": v(26.76, 4.24) * mm});
            skArc(sketch, "E15.40.23.0", {"start": v(26.62, 3.59) * mm, "mid": v(26.76, 3.8) * mm, "end": v(26.79, 4.04) * mm});
            skLineSegment(sketch, "E15.44.23.0", {"start": v(26.73, 4.43) * mm, "end": v(26.76, 4.24) * mm});
            skArc(sketch, "E15.47.23.0", {"start": v(26.73, 4.43) * mm, "mid": v(26.63, 4.66) * mm, "end": v(26.43, 4.82) * mm});
            skPoint(sketch, "E15.3.24.0", {"position": v(25.12, 10.14) * mm});
            skPoint(sketch, "E15.4.24.0", {"position": v(25.46, 9.27) * mm});
            skPoint(sketch, "E15.5.24.0", {"position": v(22.58, 7.24) * mm});
            skLineSegment(sketch, "E15.6.24.0", {"start": v(22.95, 10.24) * mm, "end": v(22.08, 9.9) * mm});
            skArc(sketch, "E15.9.24.0", {"start": v(23.51, 10.34) * mm, "mid": v(24.19, 10.31) * mm, "end": v(24.85, 10.2) * mm});
            skPoint(sketch, "E15.13.24.0", {"position": v(23.2, 10.34) * mm});
            skPoint(sketch, "E15.14.24.0", {"position": v(21.62, 9.73) * mm});
            skArc(sketch, "E15.15.24.0", {"start": v(24.4, 8.05) * mm, "mid": v(24.87, 8.52) * mm, "end": v(25.3, 9.04) * mm});
            skLineSegment(sketch, "E15.16.24.0", {"start": v(23.9, 7.75) * mm, "end": v(23.04, 7.41) * mm});
            skPoint(sketch, "E15.19.24.0", {"position": v(24.16, 7.84) * mm});
            skPoint(sketch, "E15.20.24.0", {"position": v(22.08, 7.05) * mm});
            skArc(sketch, "E15.21.24.0", {"start": v(23.04, 7.41) * mm, "mid": v(22.75, 7.15) * mm, "end": v(22.72, 6.76) * mm});
            skArc(sketch, "E15.25.24.0", {"start": v(23.51, 10.34) * mm, "mid": v(23.23, 10.32) * mm, "end": v(22.95, 10.24) * mm});
            skArc(sketch, "E15.29.24.0", {"start": v(23.9, 7.75) * mm, "mid": v(24.16, 7.87) * mm, "end": v(24.4, 8.05) * mm});
            skArc(sketch, "E15.33.24.0", {"start": v(21.41, 10.18) * mm, "mid": v(21.7, 9.91) * mm, "end": v(22.08, 9.9) * mm});
            skLineSegment(sketch, "E15.37.24.0", {"start": v(25.36, 9.52) * mm, "end": v(25.3, 9.7) * mm});
            skArc(sketch, "E15.40.24.0", {"start": v(25.3, 9.04) * mm, "mid": v(25.39, 9.28) * mm, "end": v(25.36, 9.52) * mm});
            skLineSegment(sketch, "E15.44.24.0", {"start": v(25.22, 9.9) * mm, "end": v(25.3, 9.7) * mm});
            skArc(sketch, "E15.47.24.0", {"start": v(25.22, 9.9) * mm, "mid": v(25.08, 10.1) * mm, "end": v(24.85, 10.2) * mm});
            skPoint(sketch, "E15.3.25.0", {"position": v(22.47, 15.14) * mm});
            skPoint(sketch, "E15.4.25.0", {"position": v(22.97, 14.36) * mm});
            skPoint(sketch, "E15.5.25.0", {"position": v(20.58, 11.77) * mm});
            skLineSegment(sketch, "E15.6.25.0", {"start": v(20.32, 14.79) * mm, "end": v(19.54, 14.28) * mm});
            skArc(sketch, "E15.9.25.0", {"start": v(20.85, 15) * mm, "mid": v(21.51, 15.11) * mm, "end": v(22.19, 15.15) * mm});
            skPoint(sketch, "E15.13.25.0", {"position": v(20.55, 14.93) * mm});
            skPoint(sketch, "E15.14.25.0", {"position": v(19.12, 14.01) * mm});
            skArc(sketch, "E15.15.25.0", {"start": v(22.2, 12.94) * mm, "mid": v(22.56, 13.5) * mm, "end": v(22.86, 14.1) * mm});
            skLineSegment(sketch, "E15.16.25.0", {"start": v(21.77, 12.55) * mm, "end": v(21, 12.04) * mm});
            skPoint(sketch, "E15.19.25.0", {"position": v(22, 12.7) * mm});
            skPoint(sketch, "E15.20.25.0", {"position": v(20.14, 11.48) * mm});
            skArc(sketch, "E15.21.25.0", {"start": v(21, 12.04) * mm, "mid": v(20.77, 11.73) * mm, "end": v(20.82, 11.34) * mm});
            skArc(sketch, "E15.25.25.0", {"start": v(20.85, 15) * mm, "mid": v(20.57, 14.92) * mm, "end": v(20.32, 14.79) * mm});
            skArc(sketch, "E15.29.25.0", {"start": v(21.77, 12.55) * mm, "mid": v(22, 12.73) * mm, "end": v(22.2, 12.94) * mm});
            skArc(sketch, "E15.33.25.0", {"start": v(18.83, 14.4) * mm, "mid": v(19.16, 14.2) * mm, "end": v(19.54, 14.28) * mm});
            skLineSegment(sketch, "E15.37.25.0", {"start": v(22.83, 14.59) * mm, "end": v(22.72, 14.75) * mm});
            skArc(sketch, "E15.40.25.0", {"start": v(22.86, 14.1) * mm, "mid": v(22.9, 14.35) * mm, "end": v(22.83, 14.59) * mm});
            skLineSegment(sketch, "E15.44.25.0", {"start": v(22.61, 14.92) * mm, "end": v(22.72, 14.75) * mm});
            skArc(sketch, "E15.47.25.0", {"start": v(22.61, 14.92) * mm, "mid": v(22.43, 15.09) * mm, "end": v(22.19, 15.15) * mm});
            skPoint(sketch, "E15.3.26.0", {"position": v(18.83, 19.48) * mm});
            skPoint(sketch, "E15.4.26.0", {"position": v(19.48, 18.83) * mm});
            skPoint(sketch, "E15.5.26.0", {"position": v(17.68, 15.8) * mm});
            skLineSegment(sketch, "E15.6.26.0", {"start": v(16.8, 18.69) * mm, "end": v(16.15, 18.03) * mm});
            skArc(sketch, "E15.9.26.0", {"start": v(17.27, 19.01) * mm, "mid": v(17.9, 19.26) * mm, "end": v(18.55, 19.43) * mm});
            skPoint(sketch, "E15.13.26.0", {"position": v(17, 18.88) * mm});
            skPoint(sketch, "E15.14.26.0", {"position": v(15.8, 17.68) * mm});
            skArc(sketch, "E15.15.26.0", {"start": v(19.01, 17.27) * mm, "mid": v(19.26, 17.9) * mm, "end": v(19.43, 18.55) * mm});
            skLineSegment(sketch, "E15.16.26.0", {"start": v(18.69, 16.8) * mm, "end": v(18.03, 16.15) * mm});
            skPoint(sketch, "E15.19.26.0", {"position": v(18.88, 17) * mm});
            skPoint(sketch, "E15.20.26.0", {"position": v(17.3, 15.42) * mm});
            skArc(sketch, "E15.21.26.0", {"start": v(18.03, 16.15) * mm, "mid": v(17.88, 15.79) * mm, "end": v(18, 15.42) * mm});
            skArc(sketch, "E15.25.26.0", {"start": v(17.27, 19.01) * mm, "mid": v(17.02, 18.87) * mm, "end": v(16.8, 18.69) * mm});
            skArc(sketch, "E15.29.26.0", {"start": v(18.69, 16.8) * mm, "mid": v(18.87, 17.02) * mm, "end": v(19.01, 17.27) * mm});
            skArc(sketch, "E15.33.26.0", {"start": v(15.42, 18) * mm, "mid": v(15.79, 17.88) * mm, "end": v(16.15, 18.03) * mm});
            skLineSegment(sketch, "E15.37.26.0", {"start": v(19.3, 19.02) * mm, "end": v(19.16, 19.16) * mm});
            skArc(sketch, "E15.40.26.0", {"start": v(19.43, 18.55) * mm, "mid": v(19.42, 18.8) * mm, "end": v(19.3, 19.02) * mm});
            skLineSegment(sketch, "E15.44.26.0", {"start": v(19.02, 19.3) * mm, "end": v(19.16, 19.16) * mm});
            skArc(sketch, "E15.47.26.0", {"start": v(19.02, 19.3) * mm, "mid": v(18.8, 19.42) * mm, "end": v(18.55, 19.43) * mm});
            skPoint(sketch, "E15.3.27.0", {"position": v(14.36, 22.97) * mm});
            skPoint(sketch, "E15.4.27.0", {"position": v(15.14, 22.47) * mm});
            skPoint(sketch, "E15.5.27.0", {"position": v(14.01, 19.12) * mm});
            skLineSegment(sketch, "E15.6.27.0", {"start": v(12.55, 21.77) * mm, "end": v(12.04, 21) * mm});
            skArc(sketch, "E15.9.27.0", {"start": v(12.94, 22.2) * mm, "mid": v(13.5, 22.56) * mm, "end": v(14.1, 22.86) * mm});
            skPoint(sketch, "E15.13.27.0", {"position": v(12.7, 22) * mm});
            skPoint(sketch, "E15.14.27.0", {"position": v(11.77, 20.58) * mm});
            skArc(sketch, "E15.15.27.0", {"start": v(15, 20.85) * mm, "mid": v(15.11, 21.51) * mm, "end": v(15.15, 22.19) * mm});
            skLineSegment(sketch, "E15.16.27.0", {"start": v(14.79, 20.32) * mm, "end": v(14.28, 19.54) * mm});
            skPoint(sketch, "E15.19.27.0", {"position": v(14.93, 20.55) * mm});
            skPoint(sketch, "E15.20.27.0", {"position": v(13.72, 18.68) * mm});
            skArc(sketch, "E15.21.27.0", {"start": v(14.28, 19.54) * mm, "mid": v(14.2, 19.16) * mm, "end": v(14.4, 18.83) * mm});
            skArc(sketch, "E15.25.27.0", {"start": v(12.94, 22.2) * mm, "mid": v(12.73, 22) * mm, "end": v(12.55, 21.77) * mm});
            skArc(sketch, "E15.29.27.0", {"start": v(14.79, 20.32) * mm, "mid": v(14.92, 20.57) * mm, "end": v(15, 20.85) * mm});
            skArc(sketch, "E15.33.27.0", {"start": v(11.34, 20.82) * mm, "mid": v(11.73, 20.77) * mm, "end": v(12.04, 21) * mm});
            skLineSegment(sketch, "E15.37.27.0", {"start": v(14.92, 22.61) * mm, "end": v(14.75, 22.72) * mm});
            skArc(sketch, "E15.40.27.0", {"start": v(15.15, 22.19) * mm, "mid": v(15.09, 22.43) * mm, "end": v(14.92, 22.61) * mm});
            skLineSegment(sketch, "E15.44.27.0", {"start": v(14.59, 22.83) * mm, "end": v(14.75, 22.72) * mm});
            skArc(sketch, "E15.47.27.0", {"start": v(14.59, 22.83) * mm, "mid": v(14.35, 22.9) * mm, "end": v(14.1, 22.86) * mm});
            skPoint(sketch, "E15.3.28.0", {"position": v(9.27, 25.46) * mm});
            skPoint(sketch, "E15.4.28.0", {"position": v(10.14, 25.12) * mm});
            skPoint(sketch, "E15.5.28.0", {"position": v(9.73, 21.62) * mm});
            skLineSegment(sketch, "E15.6.28.0", {"start": v(7.75, 23.9) * mm, "end": v(7.41, 23.04) * mm});
            skArc(sketch, "E15.9.28.0", {"start": v(8.05, 24.4) * mm, "mid": v(8.52, 24.87) * mm, "end": v(9.04, 25.3) * mm});
            skPoint(sketch, "E15.13.28.0", {"position": v(7.84, 24.16) * mm});
            skPoint(sketch, "E15.14.28.0", {"position": v(7.24, 22.58) * mm});
            skArc(sketch, "E15.15.28.0", {"start": v(10.34, 23.51) * mm, "mid": v(10.31, 24.19) * mm, "end": v(10.2, 24.85) * mm});
            skLineSegment(sketch, "E15.16.28.0", {"start": v(10.24, 22.95) * mm, "end": v(9.9, 22.08) * mm});
            skPoint(sketch, "E15.19.28.0", {"position": v(10.34, 23.2) * mm});
            skPoint(sketch, "E15.20.28.0", {"position": v(9.54, 21.13) * mm});
            skArc(sketch, "E15.21.28.0", {"start": v(9.9, 22.08) * mm, "mid": v(9.91, 21.7) * mm, "end": v(10.18, 21.41) * mm});
            skArc(sketch, "E15.25.28.0", {"start": v(8.05, 24.4) * mm, "mid": v(7.87, 24.16) * mm, "end": v(7.75, 23.9) * mm});
            skArc(sketch, "E15.29.28.0", {"start": v(10.24, 22.95) * mm, "mid": v(10.32, 23.23) * mm, "end": v(10.34, 23.51) * mm});
            skArc(sketch, "E15.33.28.0", {"start": v(6.76, 22.72) * mm, "mid": v(7.15, 22.75) * mm, "end": v(7.41, 23.04) * mm});
            skLineSegment(sketch, "E15.37.28.0", {"start": v(9.9, 25.22) * mm, "end": v(9.7, 25.3) * mm});
            skArc(sketch, "E15.40.28.0", {"start": v(10.2, 24.85) * mm, "mid": v(10.1, 25.08) * mm, "end": v(9.9, 25.22) * mm});
            skLineSegment(sketch, "E15.44.28.0", {"start": v(9.52, 25.36) * mm, "end": v(9.7, 25.3) * mm});
            skArc(sketch, "E15.47.28.0", {"start": v(9.52, 25.36) * mm, "mid": v(9.28, 25.39) * mm, "end": v(9.04, 25.3) * mm});
            skPoint(sketch, "E15.3.29.0", {"position": v(3.78, 26.83) * mm});
            skPoint(sketch, "E15.4.29.0", {"position": v(4.7, 26.68) * mm});
            skPoint(sketch, "E15.5.29.0", {"position": v(5.02, 23.17) * mm});
            skLineSegment(sketch, "E15.6.29.0", {"start": v(2.6, 25) * mm, "end": v(2.46, 24.08) * mm});
            skArc(sketch, "E15.9.29.0", {"start": v(2.8, 25.54) * mm, "mid": v(3.16, 26.1) * mm, "end": v(3.59, 26.62) * mm});
            skPoint(sketch, "E15.13.29.0", {"position": v(2.65, 25.26) * mm});
            skPoint(sketch, "E15.14.29.0", {"position": v(2.38, 23.59) * mm});
            skArc(sketch, "E15.15.29.0", {"start": v(5.23, 25.15) * mm, "mid": v(5.06, 25.8) * mm, "end": v(4.82, 26.43) * mm});
            skLineSegment(sketch, "E15.16.29.0", {"start": v(5.24, 24.58) * mm, "end": v(5.1, 23.66) * mm});
            skPoint(sketch, "E15.19.29.0", {"position": v(5.29, 24.84) * mm});
            skPoint(sketch, "E15.20.29.0", {"position": v(4.94, 22.65) * mm});
            skArc(sketch, "E15.21.29.0", {"start": v(5.1, 23.66) * mm, "mid": v(5.18, 23.28) * mm, "end": v(5.5, 23.06) * mm});
            skArc(sketch, "E15.25.29.0", {"start": v(2.8, 25.54) * mm, "mid": v(2.68, 25.27) * mm, "end": v(2.6, 25) * mm});
            skArc(sketch, "E15.29.29.0", {"start": v(5.24, 24.58) * mm, "mid": v(5.26, 24.86) * mm, "end": v(5.23, 25.15) * mm});
            skArc(sketch, "E15.33.29.0", {"start": v(1.9, 23.63) * mm, "mid": v(2.27, 23.74) * mm, "end": v(2.46, 24.08) * mm});
            skLineSegment(sketch, "E15.37.29.0", {"start": v(4.43, 26.73) * mm, "end": v(4.24, 26.76) * mm});
            skArc(sketch, "E15.40.29.0", {"start": v(4.82, 26.43) * mm, "mid": v(4.66, 26.63) * mm, "end": v(4.43, 26.73) * mm});
            skLineSegment(sketch, "E15.44.29.0", {"start": v(4.04, 26.79) * mm, "end": v(4.24, 26.76) * mm});
            skArc(sketch, "E15.47.29.0", {"start": v(4.04, 26.79) * mm, "mid": v(3.8, 26.76) * mm, "end": v(3.59, 26.62) * mm});
            skLineSegment(sketch, "E16", {"start": v(0.59, 23.7) * mm, "end": v(1.9, 23.63) * mm});
            skLineSegment(sketch, "E17.1.0", {"start": v(-4.35, 23.3) * mm, "end": v(-3.06, 23.5) * mm});
            skLineSegment(sketch, "E17.2.0", {"start": v(-9.1, 21.89) * mm, "end": v(-7.88, 22.36) * mm});
            skLineSegment(sketch, "E17.3.0", {"start": v(-13.45, 19.52) * mm, "end": v(-12.36, 20.23) * mm});
            skLineSegment(sketch, "E17.4.0", {"start": v(-17.22, 16.3) * mm, "end": v(-16.3, 17.22) * mm});
            skLineSegment(sketch, "E17.5.0", {"start": v(-20.23, 12.36) * mm, "end": v(-19.52, 13.45) * mm});
            skLineSegment(sketch, "E17.6.0", {"start": v(-22.36, 7.88) * mm, "end": v(-21.89, 9.1) * mm});
            skLineSegment(sketch, "E17.7.0", {"start": v(-23.5, 3.06) * mm, "end": v(-23.3, 4.35) * mm});
            skLineSegment(sketch, "E17.8.0", {"start": v(-23.63, -1.9) * mm, "end": v(-23.7, -0.59) * mm});
            skLineSegment(sketch, "E17.9.0", {"start": v(-22.72, -6.76) * mm, "end": v(-23.06, -5.5) * mm});
            skLineSegment(sketch, "E17.10.0", {"start": v(-20.82, -11.34) * mm, "end": v(-21.41, -10.18) * mm});
            skLineSegment(sketch, "E17.11.0", {"start": v(-18, -15.42) * mm, "end": v(-18.83, -14.4) * mm});
            skLineSegment(sketch, "E17.12.0", {"start": v(-14.4, -18.83) * mm, "end": v(-15.42, -18) * mm});
            skLineSegment(sketch, "E17.13.0", {"start": v(-10.18, -21.41) * mm, "end": v(-11.34, -20.82) * mm});
            skLineSegment(sketch, "E17.14.0", {"start": v(-5.5, -23.06) * mm, "end": v(-6.76, -22.72) * mm});
            skLineSegment(sketch, "E17.15.0", {"start": v(-0.59, -23.7) * mm, "end": v(-1.9, -23.63) * mm});
            skLineSegment(sketch, "E17.16.0", {"start": v(4.35, -23.3) * mm, "end": v(3.06, -23.5) * mm});
            skLineSegment(sketch, "E17.17.0", {"start": v(9.1, -21.89) * mm, "end": v(7.88, -22.36) * mm});
            skLineSegment(sketch, "E17.18.0", {"start": v(13.45, -19.52) * mm, "end": v(12.36, -20.23) * mm});
            skLineSegment(sketch, "E17.19.0", {"start": v(17.22, -16.3) * mm, "end": v(16.3, -17.22) * mm});
            skLineSegment(sketch, "E17.20.0", {"start": v(20.23, -12.36) * mm, "end": v(19.52, -13.45) * mm});
            skLineSegment(sketch, "E17.21.0", {"start": v(22.36, -7.88) * mm, "end": v(21.89, -9.1) * mm});
            skLineSegment(sketch, "E17.22.0", {"start": v(23.5, -3.06) * mm, "end": v(23.3, -4.35) * mm});
            skLineSegment(sketch, "E17.23.0", {"start": v(23.63, 1.9) * mm, "end": v(23.7, 0.59) * mm});
            skLineSegment(sketch, "E17.24.0", {"start": v(22.72, 6.76) * mm, "end": v(23.06, 5.5) * mm});
            skLineSegment(sketch, "E17.25.0", {"start": v(20.82, 11.34) * mm, "end": v(21.41, 10.18) * mm});
            skLineSegment(sketch, "E17.26.0", {"start": v(18, 15.42) * mm, "end": v(18.83, 14.4) * mm});
            skLineSegment(sketch, "E17.27.0", {"start": v(14.4, 18.83) * mm, "end": v(15.42, 18) * mm});
            skLineSegment(sketch, "E17.28.0", {"start": v(10.18, 21.41) * mm, "end": v(11.34, 20.82) * mm});
            skLineSegment(sketch, "E17.29.0", {"start": v(5.5, 23.06) * mm, "end": v(6.76, 22.72) * mm});
            skSolve(sketch);
        }
        {
            var Q0;
            Q0=makeQuery(id+"F0.imprint","IMPRINT",FACE,{"disambiguationData":[TD([[makeQuery(id+"F0.imprint","IMPRINT",EDGE,{"derivedFrom":sQuery(id+"F0.wireOp",EDGE,"E0.trimOffspring")}),1.0]])]});
            cPlane(context, id + "F1", {"entities" : qUnion([Q0]), "cplaneType" : CPlaneType.OFFSET, "offset" : 22 * mm, "width" : 152.4 * mm, "height" : 152.4 * mm});
        }
        {
            var Q0;
            Q0=qCreatedBy(id+"F1.planeOp",FACE);
            var sketch = newSketch(context, id + "F2", { "sketchPlane" : qUnion([Q0])});
            skArc(sketch, "E18.trimOffspring", {"start": v(-0.1, 38.37) * mm, "mid": v(-0.62, 39.42) * mm, "end": v(-1.27, 40.4) * mm});
            skLineSegment(sketch, "E19", {"start": v(-1.7, 40.6) * mm, "end": v(-2.13, 40.6) * mm});
            skLineSegment(sketch, "E20", {"start": v(0.02, 37.84) * mm, "end": v(0.12, 36.06) * mm});
            skLineSegment(sketch, "E21.MirrorCS", {"start": v(-2.56, 40.56) * mm, "end": v(-2.13, 40.6) * mm});
            skArc(sketch, "E22.MirrorCS", {"start": v(-3.91, 38.17) * mm, "mid": v(-3.5, 39.27) * mm, "end": v(-2.96, 40.31) * mm});
            skLineSegment(sketch, "E23.MirrorCS", {"start": v(-3.98, 37.63) * mm, "end": v(-3.88, 35.85) * mm});
            skPoint(sketch, "E24.visualSharp", {"position": v(-3.86, 35.35) * mm});
            skArc(sketch, "E24.filletArc", {"start": v(-4.35, 35.3) * mm, "mid": v(-4, 35.48) * mm, "end": v(-3.88, 35.85) * mm});
            skPoint(sketch, "E25.visualSharp", {"position": v(0.14, 35.56) * mm});
            skArc(sketch, "E25.filletArc", {"start": v(0.12, 36.06) * mm, "mid": v(0.28, 35.7) * mm, "end": v(0.64, 35.55) * mm});
            skPoint(sketch, "E26.visualSharp", {"position": v(-4, 37.9) * mm});
            skArc(sketch, "E26.filletArc", {"start": v(-3.91, 38.17) * mm, "mid": v(-3.97, 37.9) * mm, "end": v(-3.98, 37.63) * mm});
            skPoint(sketch, "E27.visualSharp", {"position": v(0, 38.1) * mm});
            skArc(sketch, "E27.filletArc", {"start": v(0.02, 37.84) * mm, "mid": v(-0.02, 38.1) * mm, "end": v(-0.1, 38.37) * mm});
            skPoint(sketch, "E28.visualSharp", {"position": v(-2.82, 40.54) * mm});
            skArc(sketch, "E28.filletArc", {"start": v(-2.56, 40.56) * mm, "mid": v(-2.8, 40.49) * mm, "end": v(-2.96, 40.31) * mm});
            skPoint(sketch, "E29.visualSharp", {"position": v(-1.43, 40.61) * mm});
            skArc(sketch, "E29.filletArc", {"start": v(-1.27, 40.4) * mm, "mid": v(-1.45, 40.56) * mm, "end": v(-1.7, 40.6) * mm});
            skPoint(sketch, "E30.1.0", {"position": v(-7.91, 37.27) * mm});
            skPoint(sketch, "E30.1.1", {"position": v(-11.12, 33.78) * mm});
            skLineSegment(sketch, "E30.1.2", {"start": v(-11.71, 35.98) * mm, "end": v(-11.25, 34.26) * mm});
            skPoint(sketch, "E30.1.3", {"position": v(-11.2, 39.07) * mm});
            skPoint(sketch, "E30.1.4", {"position": v(-9.84, 39.43) * mm});
            skArc(sketch, "E30.1.5", {"start": v(-11.76, 36.52) * mm, "mid": v(-11.6, 37.68) * mm, "end": v(-11.28, 38.82) * mm});
            skLineSegment(sketch, "E30.1.6", {"start": v(-7.84, 37.01) * mm, "end": v(-7.38, 35.3) * mm});
            skPoint(sketch, "E30.1.7", {"position": v(-7.25, 34.81) * mm});
            skPoint(sketch, "E30.1.8", {"position": v(-11.78, 36.23) * mm});
            skArc(sketch, "E30.1.9", {"start": v(-8.07, 37.5) * mm, "mid": v(-8.8, 38.43) * mm, "end": v(-9.64, 39.26) * mm});
            skArc(sketch, "E30.1.10", {"start": v(-11.6, 33.62) * mm, "mid": v(-11.3, 33.87) * mm, "end": v(-11.25, 34.26) * mm});
            skArc(sketch, "E30.1.11", {"start": v(-7.38, 35.3) * mm, "mid": v(-7.15, 34.98) * mm, "end": v(-6.77, 34.91) * mm});
            skArc(sketch, "E30.1.12", {"start": v(-9.64, 39.26) * mm, "mid": v(-9.85, 39.37) * mm, "end": v(-10.1, 39.37) * mm});
            skArc(sketch, "E30.1.13", {"start": v(-11.76, 36.52) * mm, "mid": v(-11.76, 36.25) * mm, "end": v(-11.71, 35.98) * mm});
            skLineSegment(sketch, "E30.1.14", {"start": v(-10.1, 39.37) * mm, "end": v(-10.52, 39.26) * mm});
            skArc(sketch, "E30.1.15", {"start": v(-10.94, 39.14) * mm, "mid": v(-11.15, 39.02) * mm, "end": v(-11.28, 38.82) * mm});
            skLineSegment(sketch, "E30.1.16", {"start": v(-10.94, 39.14) * mm, "end": v(-10.52, 39.26) * mm});
            skArc(sketch, "E30.1.17", {"start": v(-7.84, 37.01) * mm, "mid": v(-7.94, 37.27) * mm, "end": v(-8.07, 37.5) * mm});
            skPoint(sketch, "E30.2.0", {"position": v(-15.49, 34.8) * mm});
            skPoint(sketch, "E30.2.1", {"position": v(-17.9, 30.72) * mm});
            skLineSegment(sketch, "E30.2.2", {"start": v(-18.94, 32.76) * mm, "end": v(-18.13, 31.17) * mm});
            skPoint(sketch, "E30.2.3", {"position": v(-19.07, 35.89) * mm});
            skPoint(sketch, "E30.2.4", {"position": v(-17.83, 36.52) * mm});
            skArc(sketch, "E30.2.5", {"start": v(-19.1, 33.28) * mm, "mid": v(-19.17, 34.45) * mm, "end": v(-19.1, 35.62) * mm});
            skLineSegment(sketch, "E30.2.6", {"start": v(-15.37, 34.57) * mm, "end": v(-14.56, 32.99) * mm});
            skPoint(sketch, "E30.2.7", {"position": v(-14.33, 32.54) * mm});
            skPoint(sketch, "E30.2.8", {"position": v(-19.06, 33) * mm});
            skArc(sketch, "E30.2.9", {"start": v(-15.7, 35.01) * mm, "mid": v(-16.6, 35.76) * mm, "end": v(-17.6, 36.4) * mm});
            skArc(sketch, "E30.2.10", {"start": v(-18.33, 30.47) * mm, "mid": v(-18.1, 30.78) * mm, "end": v(-18.13, 31.17) * mm});
            skArc(sketch, "E30.2.11", {"start": v(-14.56, 32.99) * mm, "mid": v(-14.27, 32.73) * mm, "end": v(-13.88, 32.74) * mm});
            skArc(sketch, "E30.2.12", {"start": v(-17.6, 36.4) * mm, "mid": v(-17.82, 36.46) * mm, "end": v(-18.06, 36.4) * mm});
            skArc(sketch, "E30.2.13", {"start": v(-19.1, 33.28) * mm, "mid": v(-19.04, 33) * mm, "end": v(-18.94, 32.76) * mm});
            skLineSegment(sketch, "E30.2.14", {"start": v(-18.06, 36.4) * mm, "end": v(-18.45, 36.22) * mm});
            skArc(sketch, "E30.2.15", {"start": v(-18.84, 36.01) * mm, "mid": v(-19.02, 35.85) * mm, "end": v(-19.1, 35.62) * mm});
            skLineSegment(sketch, "E30.2.16", {"start": v(-18.84, 36.01) * mm, "end": v(-18.45, 36.22) * mm});
            skArc(sketch, "E30.2.17", {"start": v(-15.37, 34.57) * mm, "mid": v(-15.51, 34.8) * mm, "end": v(-15.7, 35.01) * mm});
            skPoint(sketch, "E30.center", {"position": v(0, 0) * mm});
            skPoint(sketch, "E31.1.3.0", {"position": v(-23.9, 26.33) * mm});
            skLineSegment(sketch, "E31.2.3.0", {"start": v(-25.33, 28.1) * mm, "end": v(-24.21, 26.72) * mm});
            skPoint(sketch, "E31.5.3.0", {"position": v(-26.11, 31.14) * mm});
            skPoint(sketch, "E31.6.3.0", {"position": v(-25.03, 32.02) * mm});
            skArc(sketch, "E31.7.3.0", {"start": v(-25.6, 28.58) * mm, "mid": v(-25.92, 29.71) * mm, "end": v(-26.1, 30.87) * mm});
            skLineSegment(sketch, "E31.11.3.0", {"start": v(-22.22, 30.62) * mm, "end": v(-21.1, 29.24) * mm});
            skPoint(sketch, "E31.14.3.0", {"position": v(-20.79, 28.85) * mm});
            skPoint(sketch, "E31.15.3.0", {"position": v(-25.5, 28.3) * mm});
            skArc(sketch, "E31.16.3.0", {"start": v(-22.63, 30.98) * mm, "mid": v(-23.67, 31.53) * mm, "end": v(-24.77, 31.94) * mm});
            skPoint(sketch, "E31.17.3.0", {"position": v(-22.39, 30.83) * mm});
            skArc(sketch, "E31.20.3.0", {"start": v(-24.27, 26) * mm, "mid": v(-24.1, 26.35) * mm, "end": v(-24.21, 26.72) * mm});
            skArc(sketch, "E31.24.3.0", {"start": v(-21.1, 29.24) * mm, "mid": v(-20.76, 29.05) * mm, "end": v(-20.38, 29.14) * mm});
            skArc(sketch, "E31.28.3.0", {"start": v(-24.77, 31.94) * mm, "mid": v(-25.01, 31.96) * mm, "end": v(-25.23, 31.86) * mm});
            skArc(sketch, "E31.32.3.0", {"start": v(-25.6, 28.58) * mm, "mid": v(-25.49, 28.33) * mm, "end": v(-25.33, 28.1) * mm});
            skLineSegment(sketch, "E31.36.3.0", {"start": v(-25.23, 31.86) * mm, "end": v(-25.58, 31.59) * mm});
            skArc(sketch, "E31.39.3.0", {"start": v(-25.91, 31.3) * mm, "mid": v(-26.06, 31.11) * mm, "end": v(-26.1, 30.87) * mm});
            skLineSegment(sketch, "E31.43.3.0", {"start": v(-25.91, 31.3) * mm, "end": v(-25.58, 31.59) * mm});
            skArc(sketch, "E31.46.3.0", {"start": v(-22.22, 30.62) * mm, "mid": v(-22.41, 30.82) * mm, "end": v(-22.63, 30.98) * mm});
            skPoint(sketch, "E31.1.4.0", {"position": v(-28.85, 20.79) * mm});
            skLineSegment(sketch, "E31.2.4.0", {"start": v(-30.62, 22.22) * mm, "end": v(-29.24, 21.1) * mm});
            skPoint(sketch, "E31.5.4.0", {"position": v(-32.02, 25.03) * mm});
            skPoint(sketch, "E31.6.4.0", {"position": v(-31.14, 26.11) * mm});
            skArc(sketch, "E31.7.4.0", {"start": v(-30.98, 22.63) * mm, "mid": v(-31.53, 23.67) * mm, "end": v(-31.94, 24.77) * mm});
            skLineSegment(sketch, "E31.11.4.0", {"start": v(-28.1, 25.33) * mm, "end": v(-26.72, 24.21) * mm});
            skPoint(sketch, "E31.14.4.0", {"position": v(-26.33, 23.9) * mm});
            skPoint(sketch, "E31.15.4.0", {"position": v(-30.83, 22.39) * mm});
            skArc(sketch, "E31.16.4.0", {"start": v(-28.58, 25.6) * mm, "mid": v(-29.71, 25.92) * mm, "end": v(-30.87, 26.1) * mm});
            skPoint(sketch, "E31.17.4.0", {"position": v(-28.3, 25.5) * mm});
            skArc(sketch, "E31.20.4.0", {"start": v(-29.14, 20.38) * mm, "mid": v(-29.05, 20.76) * mm, "end": v(-29.24, 21.1) * mm});
            skArc(sketch, "E31.24.4.0", {"start": v(-26.72, 24.21) * mm, "mid": v(-26.35, 24.1) * mm, "end": v(-26, 24.27) * mm});
            skArc(sketch, "E31.28.4.0", {"start": v(-30.87, 26.1) * mm, "mid": v(-31.11, 26.06) * mm, "end": v(-31.3, 25.91) * mm});
            skArc(sketch, "E31.32.4.0", {"start": v(-30.98, 22.63) * mm, "mid": v(-30.82, 22.41) * mm, "end": v(-30.62, 22.22) * mm});
            skLineSegment(sketch, "E31.36.4.0", {"start": v(-31.3, 25.91) * mm, "end": v(-31.59, 25.58) * mm});
            skArc(sketch, "E31.39.4.0", {"start": v(-31.86, 25.23) * mm, "mid": v(-31.96, 25.01) * mm, "end": v(-31.94, 24.77) * mm});
            skLineSegment(sketch, "E31.43.4.0", {"start": v(-31.86, 25.23) * mm, "end": v(-31.59, 25.58) * mm});
            skArc(sketch, "E31.46.4.0", {"start": v(-28.1, 25.33) * mm, "mid": v(-28.33, 25.49) * mm, "end": v(-28.58, 25.6) * mm});
            skPoint(sketch, "E31.1.5.0", {"position": v(-32.54, 14.33) * mm});
            skLineSegment(sketch, "E31.2.5.0", {"start": v(-34.57, 15.37) * mm, "end": v(-32.99, 14.56) * mm});
            skPoint(sketch, "E31.5.5.0", {"position": v(-36.52, 17.83) * mm});
            skPoint(sketch, "E31.6.5.0", {"position": v(-35.89, 19.07) * mm});
            skArc(sketch, "E31.7.5.0", {"start": v(-35.01, 15.7) * mm, "mid": v(-35.76, 16.6) * mm, "end": v(-36.4, 17.6) * mm});
            skLineSegment(sketch, "E31.11.5.0", {"start": v(-32.76, 18.94) * mm, "end": v(-31.17, 18.13) * mm});
            skPoint(sketch, "E31.14.5.0", {"position": v(-30.72, 17.9) * mm});
            skPoint(sketch, "E31.15.5.0", {"position": v(-34.8, 15.49) * mm});
            skArc(sketch, "E31.16.5.0", {"start": v(-33.28, 19.1) * mm, "mid": v(-34.45, 19.17) * mm, "end": v(-35.62, 19.1) * mm});
            skPoint(sketch, "E31.17.5.0", {"position": v(-33, 19.06) * mm});
            skArc(sketch, "E31.20.5.0", {"start": v(-32.74, 13.88) * mm, "mid": v(-32.73, 14.27) * mm, "end": v(-32.99, 14.56) * mm});
            skArc(sketch, "E31.24.5.0", {"start": v(-31.17, 18.13) * mm, "mid": v(-30.78, 18.1) * mm, "end": v(-30.47, 18.33) * mm});
            skArc(sketch, "E31.28.5.0", {"start": v(-35.62, 19.1) * mm, "mid": v(-35.85, 19.02) * mm, "end": v(-36.01, 18.84) * mm});
            skArc(sketch, "E31.32.5.0", {"start": v(-35.01, 15.7) * mm, "mid": v(-34.8, 15.51) * mm, "end": v(-34.57, 15.37) * mm});
            skLineSegment(sketch, "E31.36.5.0", {"start": v(-36.01, 18.84) * mm, "end": v(-36.22, 18.45) * mm});
            skArc(sketch, "E31.39.5.0", {"start": v(-36.4, 18.06) * mm, "mid": v(-36.46, 17.82) * mm, "end": v(-36.4, 17.6) * mm});
            skLineSegment(sketch, "E31.43.5.0", {"start": v(-36.4, 18.06) * mm, "end": v(-36.22, 18.45) * mm});
            skArc(sketch, "E31.46.5.0", {"start": v(-32.76, 18.94) * mm, "mid": v(-33, 19.04) * mm, "end": v(-33.28, 19.1) * mm});
            skPoint(sketch, "E31.1.6.0", {"position": v(-34.81, 7.25) * mm});
            skLineSegment(sketch, "E31.2.6.0", {"start": v(-37.01, 7.84) * mm, "end": v(-35.3, 7.38) * mm});
            skPoint(sketch, "E31.5.6.0", {"position": v(-39.43, 9.84) * mm});
            skPoint(sketch, "E31.6.6.0", {"position": v(-39.07, 11.2) * mm});
            skArc(sketch, "E31.7.6.0", {"start": v(-37.5, 8.07) * mm, "mid": v(-38.43, 8.8) * mm, "end": v(-39.26, 9.64) * mm});
            skLineSegment(sketch, "E31.11.6.0", {"start": v(-35.98, 11.71) * mm, "end": v(-34.26, 11.25) * mm});
            skPoint(sketch, "E31.14.6.0", {"position": v(-33.78, 11.12) * mm});
            skPoint(sketch, "E31.15.6.0", {"position": v(-37.27, 7.91) * mm});
            skArc(sketch, "E31.16.6.0", {"start": v(-36.52, 11.76) * mm, "mid": v(-37.68, 11.6) * mm, "end": v(-38.82, 11.28) * mm});
            skPoint(sketch, "E31.17.6.0", {"position": v(-36.23, 11.78) * mm});
            skArc(sketch, "E31.20.6.0", {"start": v(-34.91, 6.77) * mm, "mid": v(-34.98, 7.15) * mm, "end": v(-35.3, 7.38) * mm});
            skArc(sketch, "E31.24.6.0", {"start": v(-34.26, 11.25) * mm, "mid": v(-33.87, 11.3) * mm, "end": v(-33.62, 11.6) * mm});
            skArc(sketch, "E31.28.6.0", {"start": v(-38.82, 11.28) * mm, "mid": v(-39.02, 11.15) * mm, "end": v(-39.14, 10.94) * mm});
            skArc(sketch, "E31.32.6.0", {"start": v(-37.5, 8.07) * mm, "mid": v(-37.27, 7.94) * mm, "end": v(-37.01, 7.84) * mm});
            skLineSegment(sketch, "E31.36.6.0", {"start": v(-39.14, 10.94) * mm, "end": v(-39.26, 10.52) * mm});
            skArc(sketch, "E31.39.6.0", {"start": v(-39.37, 10.1) * mm, "mid": v(-39.37, 9.85) * mm, "end": v(-39.26, 9.64) * mm});
            skLineSegment(sketch, "E31.43.6.0", {"start": v(-39.37, 10.1) * mm, "end": v(-39.26, 10.52) * mm});
            skArc(sketch, "E31.46.6.0", {"start": v(-35.98, 11.71) * mm, "mid": v(-36.25, 11.76) * mm, "end": v(-36.52, 11.76) * mm});
            skPoint(sketch, "E31.1.7.0", {"position": v(-35.56, -0.14) * mm});
            skLineSegment(sketch, "E31.2.7.0", {"start": v(-37.84, -0.02) * mm, "end": v(-36.06, -0.12) * mm});
            skPoint(sketch, "E31.5.7.0", {"position": v(-40.61, 1.43) * mm});
            skPoint(sketch, "E31.6.7.0", {"position": v(-40.54, 2.82) * mm});
            skArc(sketch, "E31.7.7.0", {"start": v(-38.37, 0.1) * mm, "mid": v(-39.42, 0.62) * mm, "end": v(-40.4, 1.27) * mm});
            skLineSegment(sketch, "E31.11.7.0", {"start": v(-37.63, 3.98) * mm, "end": v(-35.85, 3.88) * mm});
            skPoint(sketch, "E31.14.7.0", {"position": v(-35.35, 3.86) * mm});
            skPoint(sketch, "E31.15.7.0", {"position": v(-38.1, 0) * mm});
            skArc(sketch, "E31.16.7.0", {"start": v(-38.17, 3.91) * mm, "mid": v(-39.27, 3.5) * mm, "end": v(-40.31, 2.96) * mm});
            skPoint(sketch, "E31.17.7.0", {"position": v(-37.9, 4) * mm});
            skArc(sketch, "E31.20.7.0", {"start": v(-35.55, -0.64) * mm, "mid": v(-35.7, -0.28) * mm, "end": v(-36.06, -0.12) * mm});
            skArc(sketch, "E31.24.7.0", {"start": v(-35.85, 3.88) * mm, "mid": v(-35.48, 4) * mm, "end": v(-35.3, 4.35) * mm});
            skArc(sketch, "E31.28.7.0", {"start": v(-40.31, 2.96) * mm, "mid": v(-40.49, 2.8) * mm, "end": v(-40.56, 2.56) * mm});
            skArc(sketch, "E31.32.7.0", {"start": v(-38.37, 0.1) * mm, "mid": v(-38.1, 0.02) * mm, "end": v(-37.84, -0.02) * mm});
            skLineSegment(sketch, "E31.36.7.0", {"start": v(-40.56, 2.56) * mm, "end": v(-40.6, 2.13) * mm});
            skArc(sketch, "E31.39.7.0", {"start": v(-40.6, 1.7) * mm, "mid": v(-40.56, 1.45) * mm, "end": v(-40.4, 1.27) * mm});
            skLineSegment(sketch, "E31.43.7.0", {"start": v(-40.6, 1.7) * mm, "end": v(-40.6, 2.13) * mm});
            skArc(sketch, "E31.46.7.0", {"start": v(-37.63, 3.98) * mm, "mid": v(-37.9, 3.97) * mm, "end": v(-38.17, 3.91) * mm});
            skPoint(sketch, "E31.1.8.0", {"position": v(-34.75, -7.53) * mm});
            skLineSegment(sketch, "E31.2.8.0", {"start": v(-37, -7.89) * mm, "end": v(-35.25, -7.61) * mm});
            skPoint(sketch, "E31.5.8.0", {"position": v(-40.02, -7.05) * mm});
            skPoint(sketch, "E31.6.8.0", {"position": v(-40.24, -5.67) * mm});
            skArc(sketch, "E31.7.8.0", {"start": v(-37.55, -7.88) * mm, "mid": v(-38.69, -7.6) * mm, "end": v(-39.78, -7.16) * mm});
            skLineSegment(sketch, "E31.11.8.0", {"start": v(-37.63, -3.93) * mm, "end": v(-35.87, -3.65) * mm});
            skPoint(sketch, "E31.14.8.0", {"position": v(-35.38, -3.58) * mm});
            skPoint(sketch, "E31.15.8.0", {"position": v(-37.27, -7.93) * mm});
            skArc(sketch, "E31.16.8.0", {"start": v(-38.15, -4.1) * mm, "mid": v(-39.14, -4.74) * mm, "end": v(-40.05, -5.48) * mm});
            skPoint(sketch, "E31.17.8.0", {"position": v(-37.9, -3.97) * mm});
            skArc(sketch, "E31.20.8.0", {"start": v(-34.64, -8.02) * mm, "mid": v(-34.87, -7.7) * mm, "end": v(-35.25, -7.61) * mm});
            skArc(sketch, "E31.24.8.0", {"start": v(-35.87, -3.65) * mm, "mid": v(-35.54, -3.46) * mm, "end": v(-35.43, -3.08) * mm});
            skArc(sketch, "E31.28.8.0", {"start": v(-40.05, -5.48) * mm, "mid": v(-40.18, -5.68) * mm, "end": v(-40.2, -5.93) * mm});
            skArc(sketch, "E31.32.8.0", {"start": v(-37.55, -7.88) * mm, "mid": v(-37.28, -7.9) * mm, "end": v(-37, -7.89) * mm});
            skLineSegment(sketch, "E31.36.8.0", {"start": v(-40.2, -5.93) * mm, "end": v(-40.15, -6.36) * mm});
            skArc(sketch, "E31.39.8.0", {"start": v(-40.07, -6.79) * mm, "mid": v(-39.97, -7.01) * mm, "end": v(-39.78, -7.16) * mm});
            skLineSegment(sketch, "E31.43.8.0", {"start": v(-40.07, -6.79) * mm, "end": v(-40.15, -6.36) * mm});
            skArc(sketch, "E31.46.8.0", {"start": v(-37.63, -3.93) * mm, "mid": v(-37.9, -4) * mm, "end": v(-38.15, -4.1) * mm});
            skPoint(sketch, "E31.1.9.0", {"position": v(-32.43, -14.6) * mm});
            skLineSegment(sketch, "E31.2.9.0", {"start": v(-34.56, -15.41) * mm, "end": v(-32.9, -14.77) * mm});
            skPoint(sketch, "E31.5.9.0", {"position": v(-37.69, -15.21) * mm});
            skPoint(sketch, "E31.6.9.0", {"position": v(-38.19, -13.91) * mm});
            skArc(sketch, "E31.7.9.0", {"start": v(-35.1, -15.52) * mm, "mid": v(-36.27, -15.47) * mm, "end": v(-37.43, -15.28) * mm});
            skLineSegment(sketch, "E31.11.9.0", {"start": v(-36, -11.67) * mm, "end": v(-34.33, -11.03) * mm});
            skPoint(sketch, "E31.14.9.0", {"position": v(-33.86, -10.85) * mm});
            skPoint(sketch, "E31.15.9.0", {"position": v(-34.8, -15.5) * mm});
            skArc(sketch, "E31.16.9.0", {"start": v(-36.46, -11.95) * mm, "mid": v(-37.3, -12.77) * mm, "end": v(-38.03, -13.69) * mm});
            skPoint(sketch, "E31.17.9.0", {"position": v(-36.24, -11.77) * mm});
            skArc(sketch, "E31.20.9.0", {"start": v(-32.22, -15.04) * mm, "mid": v(-32.5, -14.78) * mm, "end": v(-32.9, -14.77) * mm});
            skArc(sketch, "E31.24.9.0", {"start": v(-34.33, -11.03) * mm, "mid": v(-34.04, -10.77) * mm, "end": v(-34.01, -10.38) * mm});
            skArc(sketch, "E31.28.9.0", {"start": v(-38.03, -13.69) * mm, "mid": v(-38.12, -13.91) * mm, "end": v(-38.1, -14.16) * mm});
            skArc(sketch, "E31.32.9.0", {"start": v(-35.1, -15.52) * mm, "mid": v(-34.82, -15.49) * mm, "end": v(-34.56, -15.41) * mm});
            skLineSegment(sketch, "E31.36.9.0", {"start": v(-38.1, -14.16) * mm, "end": v(-37.95, -14.57) * mm});
            skArc(sketch, "E31.39.9.0", {"start": v(-37.78, -14.97) * mm, "mid": v(-37.64, -15.17) * mm, "end": v(-37.43, -15.28) * mm});
            skLineSegment(sketch, "E31.43.9.0", {"start": v(-37.78, -14.97) * mm, "end": v(-37.95, -14.57) * mm});
            skArc(sketch, "E31.46.9.0", {"start": v(-36, -11.67) * mm, "mid": v(-36.24, -11.8) * mm, "end": v(-36.46, -11.95) * mm});
            skPoint(sketch, "E31.1.10.0", {"position": v(-28.69, -21.02) * mm});
            skLineSegment(sketch, "E31.2.10.0", {"start": v(-30.6, -22.26) * mm, "end": v(-29.1, -21.29) * mm});
            skPoint(sketch, "E31.5.10.0", {"position": v(-33.7, -22.72) * mm});
            skPoint(sketch, "E31.6.10.0", {"position": v(-34.46, -21.55) * mm});
            skArc(sketch, "E31.7.10.0", {"start": v(-31.1, -22.47) * mm, "mid": v(-32.26, -22.67) * mm, "end": v(-33.43, -22.72) * mm});
            skLineSegment(sketch, "E31.11.10.0", {"start": v(-32.78, -18.9) * mm, "end": v(-31.29, -17.93) * mm});
            skPoint(sketch, "E31.14.10.0", {"position": v(-30.87, -17.66) * mm});
            skPoint(sketch, "E31.15.10.0", {"position": v(-30.82, -22.4) * mm});
            skArc(sketch, "E31.16.10.0", {"start": v(-33.18, -19.27) * mm, "mid": v(-33.83, -20.25) * mm, "end": v(-34.36, -21.3) * mm});
            skPoint(sketch, "E31.17.10.0", {"position": v(-33, -19.04) * mm});
            skArc(sketch, "E31.20.10.0", {"start": v(-28.39, -21.41) * mm, "mid": v(-28.72, -21.21) * mm, "end": v(-29.1, -21.29) * mm});
            skArc(sketch, "E31.24.10.0", {"start": v(-31.29, -17.93) * mm, "mid": v(-31.06, -17.61) * mm, "end": v(-31.11, -17.22) * mm});
            skArc(sketch, "E31.28.10.0", {"start": v(-34.36, -21.3) * mm, "mid": v(-34.4, -21.54) * mm, "end": v(-34.32, -21.77) * mm});
            skArc(sketch, "E31.32.10.0", {"start": v(-31.1, -22.47) * mm, "mid": v(-30.84, -22.39) * mm, "end": v(-30.6, -22.26) * mm});
            skLineSegment(sketch, "E31.36.10.0", {"start": v(-34.32, -21.77) * mm, "end": v(-34.09, -22.14) * mm});
            skArc(sketch, "E31.39.10.0", {"start": v(-33.84, -22.5) * mm, "mid": v(-33.67, -22.66) * mm, "end": v(-33.43, -22.72) * mm});
            skLineSegment(sketch, "E31.43.10.0", {"start": v(-33.84, -22.5) * mm, "end": v(-34.09, -22.14) * mm});
            skArc(sketch, "E31.46.10.0", {"start": v(-32.78, -18.9) * mm, "mid": v(-33, -19.07) * mm, "end": v(-33.18, -19.27) * mm});
            skPoint(sketch, "E31.1.11.0", {"position": v(-23.69, -26.52) * mm});
            skLineSegment(sketch, "E31.2.11.0", {"start": v(-25.3, -28.13) * mm, "end": v(-24.04, -26.87) * mm});
            skPoint(sketch, "E31.5.11.0", {"position": v(-28.24, -29.23) * mm});
            skPoint(sketch, "E31.6.11.0", {"position": v(-29.23, -28.24) * mm});
            skArc(sketch, "E31.7.11.0", {"start": v(-25.75, -28.45) * mm, "mid": v(-26.84, -28.88) * mm, "end": v(-27.98, -29.18) * mm});
            skLineSegment(sketch, "E31.11.11.0", {"start": v(-28.13, -25.3) * mm, "end": v(-26.87, -24.04) * mm});
            skPoint(sketch, "E31.14.11.0", {"position": v(-26.52, -23.69) * mm});
            skPoint(sketch, "E31.15.11.0", {"position": v(-25.49, -28.32) * mm});
            skArc(sketch, "E31.16.11.0", {"start": v(-28.45, -25.75) * mm, "mid": v(-28.88, -26.84) * mm, "end": v(-29.18, -27.98) * mm});
            skPoint(sketch, "E31.17.11.0", {"position": v(-28.32, -25.49) * mm});
            skArc(sketch, "E31.20.11.0", {"start": v(-23.32, -26.85) * mm, "mid": v(-23.68, -26.72) * mm, "end": v(-24.04, -26.87) * mm});
            skArc(sketch, "E31.24.11.0", {"start": v(-26.87, -24.04) * mm, "mid": v(-26.72, -23.68) * mm, "end": v(-26.85, -23.32) * mm});
            skArc(sketch, "E31.28.11.0", {"start": v(-29.18, -27.98) * mm, "mid": v(-29.17, -28.22) * mm, "end": v(-29.04, -28.43) * mm});
            skArc(sketch, "E31.32.11.0", {"start": v(-25.75, -28.45) * mm, "mid": v(-25.51, -28.3) * mm, "end": v(-25.3, -28.13) * mm});
            skLineSegment(sketch, "E31.36.11.0", {"start": v(-29.04, -28.43) * mm, "end": v(-28.74, -28.74) * mm});
            skArc(sketch, "E31.39.11.0", {"start": v(-28.43, -29.04) * mm, "mid": v(-28.22, -29.17) * mm, "end": v(-27.98, -29.18) * mm});
            skLineSegment(sketch, "E31.43.11.0", {"start": v(-28.43, -29.04) * mm, "end": v(-28.74, -28.74) * mm});
            skArc(sketch, "E31.46.11.0", {"start": v(-28.13, -25.3) * mm, "mid": v(-28.3, -25.51) * mm, "end": v(-28.45, -25.75) * mm});
            skPoint(sketch, "E31.1.12.0", {"position": v(-17.66, -30.87) * mm});
            skLineSegment(sketch, "E31.2.12.0", {"start": v(-18.9, -32.78) * mm, "end": v(-17.93, -31.29) * mm});
            skPoint(sketch, "E31.5.12.0", {"position": v(-21.55, -34.46) * mm});
            skPoint(sketch, "E31.6.12.0", {"position": v(-22.72, -33.7) * mm});
            skArc(sketch, "E31.7.12.0", {"start": v(-19.27, -33.18) * mm, "mid": v(-20.25, -33.83) * mm, "end": v(-21.3, -34.36) * mm});
            skLineSegment(sketch, "E31.11.12.0", {"start": v(-22.26, -30.6) * mm, "end": v(-21.29, -29.1) * mm});
            skPoint(sketch, "E31.14.12.0", {"position": v(-21.02, -28.69) * mm});
            skPoint(sketch, "E31.15.12.0", {"position": v(-19.04, -33) * mm});
            skArc(sketch, "E31.16.12.0", {"start": v(-22.47, -31.1) * mm, "mid": v(-22.67, -32.26) * mm, "end": v(-22.72, -33.43) * mm});
            skPoint(sketch, "E31.17.12.0", {"position": v(-22.4, -30.82) * mm});
            skArc(sketch, "E31.20.12.0", {"start": v(-17.22, -31.11) * mm, "mid": v(-17.61, -31.06) * mm, "end": v(-17.93, -31.29) * mm});
            skArc(sketch, "E31.24.12.0", {"start": v(-21.29, -29.1) * mm, "mid": v(-21.21, -28.72) * mm, "end": v(-21.41, -28.39) * mm});
            skArc(sketch, "E31.28.12.0", {"start": v(-22.72, -33.43) * mm, "mid": v(-22.66, -33.67) * mm, "end": v(-22.5, -33.84) * mm});
            skArc(sketch, "E31.32.12.0", {"start": v(-19.27, -33.18) * mm, "mid": v(-19.07, -33) * mm, "end": v(-18.9, -32.78) * mm});
            skLineSegment(sketch, "E31.36.12.0", {"start": v(-22.5, -33.84) * mm, "end": v(-22.14, -34.09) * mm});
            skArc(sketch, "E31.39.12.0", {"start": v(-21.77, -34.32) * mm, "mid": v(-21.54, -34.4) * mm, "end": v(-21.3, -34.36) * mm});
            skLineSegment(sketch, "E31.43.12.0", {"start": v(-21.77, -34.32) * mm, "end": v(-22.14, -34.09) * mm});
            skArc(sketch, "E31.46.12.0", {"start": v(-22.26, -30.6) * mm, "mid": v(-22.39, -30.84) * mm, "end": v(-22.47, -31.1) * mm});
            skPoint(sketch, "E31.1.13.0", {"position": v(-10.85, -33.86) * mm});
            skLineSegment(sketch, "E31.2.13.0", {"start": v(-11.67, -36) * mm, "end": v(-11.03, -34.33) * mm});
            skPoint(sketch, "E31.5.13.0", {"position": v(-13.91, -38.19) * mm});
            skPoint(sketch, "E31.6.13.0", {"position": v(-15.21, -37.69) * mm});
            skArc(sketch, "E31.7.13.0", {"start": v(-11.95, -36.46) * mm, "mid": v(-12.77, -37.3) * mm, "end": v(-13.69, -38.03) * mm});
            skLineSegment(sketch, "E31.11.13.0", {"start": v(-15.41, -34.56) * mm, "end": v(-14.77, -32.9) * mm});
            skPoint(sketch, "E31.14.13.0", {"position": v(-14.6, -32.43) * mm});
            skPoint(sketch, "E31.15.13.0", {"position": v(-11.77, -36.24) * mm});
            skArc(sketch, "E31.16.13.0", {"start": v(-15.52, -35.1) * mm, "mid": v(-15.47, -36.27) * mm, "end": v(-15.28, -37.43) * mm});
            skPoint(sketch, "E31.17.13.0", {"position": v(-15.5, -34.8) * mm});
            skArc(sketch, "E31.20.13.0", {"start": v(-10.38, -34.01) * mm, "mid": v(-10.77, -34.04) * mm, "end": v(-11.03, -34.33) * mm});
            skArc(sketch, "E31.24.13.0", {"start": v(-14.77, -32.9) * mm, "mid": v(-14.78, -32.5) * mm, "end": v(-15.04, -32.22) * mm});
            skArc(sketch, "E31.28.13.0", {"start": v(-15.28, -37.43) * mm, "mid": v(-15.17, -37.64) * mm, "end": v(-14.97, -37.78) * mm});
            skArc(sketch, "E31.32.13.0", {"start": v(-11.95, -36.46) * mm, "mid": v(-11.8, -36.24) * mm, "end": v(-11.67, -36) * mm});
            skLineSegment(sketch, "E31.36.13.0", {"start": v(-14.97, -37.78) * mm, "end": v(-14.57, -37.95) * mm});
            skArc(sketch, "E31.39.13.0", {"start": v(-14.16, -38.1) * mm, "mid": v(-13.91, -38.12) * mm, "end": v(-13.69, -38.03) * mm});
            skLineSegment(sketch, "E31.43.13.0", {"start": v(-14.16, -38.1) * mm, "end": v(-14.57, -37.95) * mm});
            skArc(sketch, "E31.46.13.0", {"start": v(-15.41, -34.56) * mm, "mid": v(-15.49, -34.82) * mm, "end": v(-15.52, -35.1) * mm});
            skPoint(sketch, "E31.1.14.0", {"position": v(-3.58, -35.38) * mm});
            skLineSegment(sketch, "E31.2.14.0", {"start": v(-3.93, -37.63) * mm, "end": v(-3.65, -35.87) * mm});
            skPoint(sketch, "E31.5.14.0", {"position": v(-5.67, -40.24) * mm});
            skPoint(sketch, "E31.6.14.0", {"position": v(-7.05, -40.02) * mm});
            skArc(sketch, "E31.7.14.0", {"start": v(-4.1, -38.15) * mm, "mid": v(-4.74, -39.14) * mm, "end": v(-5.48, -40.05) * mm});
            skLineSegment(sketch, "E31.11.14.0", {"start": v(-7.89, -37) * mm, "end": v(-7.61, -35.25) * mm});
            skPoint(sketch, "E31.14.14.0", {"position": v(-7.53, -34.75) * mm});
            skPoint(sketch, "E31.15.14.0", {"position": v(-3.97, -37.9) * mm});
            skArc(sketch, "E31.16.14.0", {"start": v(-7.88, -37.55) * mm, "mid": v(-7.6, -38.69) * mm, "end": v(-7.16, -39.78) * mm});
            skPoint(sketch, "E31.17.14.0", {"position": v(-7.93, -37.27) * mm});
            skArc(sketch, "E31.20.14.0", {"start": v(-3.08, -35.43) * mm, "mid": v(-3.46, -35.54) * mm, "end": v(-3.65, -35.87) * mm});
            skArc(sketch, "E31.24.14.0", {"start": v(-7.61, -35.25) * mm, "mid": v(-7.7, -34.87) * mm, "end": v(-8.02, -34.64) * mm});
            skArc(sketch, "E31.28.14.0", {"start": v(-7.16, -39.78) * mm, "mid": v(-7.01, -39.97) * mm, "end": v(-6.79, -40.07) * mm});
            skArc(sketch, "E31.32.14.0", {"start": v(-4.1, -38.15) * mm, "mid": v(-4, -37.9) * mm, "end": v(-3.93, -37.63) * mm});
            skLineSegment(sketch, "E31.36.14.0", {"start": v(-6.79, -40.07) * mm, "end": v(-6.36, -40.15) * mm});
            skArc(sketch, "E31.39.14.0", {"start": v(-5.93, -40.2) * mm, "mid": v(-5.68, -40.18) * mm, "end": v(-5.48, -40.05) * mm});
            skLineSegment(sketch, "E31.43.14.0", {"start": v(-5.93, -40.2) * mm, "end": v(-6.36, -40.15) * mm});
            skArc(sketch, "E31.46.14.0", {"start": v(-7.89, -37) * mm, "mid": v(-7.9, -37.28) * mm, "end": v(-7.88, -37.55) * mm});
            skPoint(sketch, "E31.1.15.0", {"position": v(3.86, -35.35) * mm});
            skLineSegment(sketch, "E31.2.15.0", {"start": v(3.98, -37.63) * mm, "end": v(3.88, -35.85) * mm});
            skPoint(sketch, "E31.5.15.0", {"position": v(2.82, -40.54) * mm});
            skPoint(sketch, "E31.6.15.0", {"position": v(1.43, -40.61) * mm});
            skArc(sketch, "E31.7.15.0", {"start": v(3.91, -38.17) * mm, "mid": v(3.5, -39.27) * mm, "end": v(2.96, -40.31) * mm});
            skLineSegment(sketch, "E31.11.15.0", {"start": v(-0.02, -37.84) * mm, "end": v(-0.12, -36.06) * mm});
            skPoint(sketch, "E31.14.15.0", {"position": v(-0.14, -35.56) * mm});
            skPoint(sketch, "E31.15.15.0", {"position": v(4, -37.9) * mm});
            skArc(sketch, "E31.16.15.0", {"start": v(0.1, -38.37) * mm, "mid": v(0.62, -39.42) * mm, "end": v(1.27, -40.4) * mm});
            skPoint(sketch, "E31.17.15.0", {"position": v(0, -38.1) * mm});
            skArc(sketch, "E31.20.15.0", {"start": v(4.35, -35.3) * mm, "mid": v(4, -35.48) * mm, "end": v(3.88, -35.85) * mm});
            skArc(sketch, "E31.24.15.0", {"start": v(-0.12, -36.06) * mm, "mid": v(-0.28, -35.7) * mm, "end": v(-0.64, -35.55) * mm});
            skArc(sketch, "E31.28.15.0", {"start": v(1.27, -40.4) * mm, "mid": v(1.45, -40.56) * mm, "end": v(1.7, -40.6) * mm});
            skArc(sketch, "E31.32.15.0", {"start": v(3.91, -38.17) * mm, "mid": v(3.97, -37.9) * mm, "end": v(3.98, -37.63) * mm});
            skLineSegment(sketch, "E31.36.15.0", {"start": v(1.7, -40.6) * mm, "end": v(2.13, -40.6) * mm});
            skArc(sketch, "E31.39.15.0", {"start": v(2.56, -40.56) * mm, "mid": v(2.8, -40.49) * mm, "end": v(2.96, -40.31) * mm});
            skLineSegment(sketch, "E31.43.15.0", {"start": v(2.56, -40.56) * mm, "end": v(2.13, -40.6) * mm});
            skArc(sketch, "E31.46.15.0", {"start": v(-0.02, -37.84) * mm, "mid": v(0.02, -38.1) * mm, "end": v(0.1, -38.37) * mm});
            skPoint(sketch, "E31.1.16.0", {"position": v(11.12, -33.78) * mm});
            skLineSegment(sketch, "E31.2.16.0", {"start": v(11.71, -35.98) * mm, "end": v(11.25, -34.26) * mm});
            skPoint(sketch, "E31.5.16.0", {"position": v(11.2, -39.07) * mm});
            skPoint(sketch, "E31.6.16.0", {"position": v(9.84, -39.43) * mm});
            skArc(sketch, "E31.7.16.0", {"start": v(11.76, -36.52) * mm, "mid": v(11.6, -37.68) * mm, "end": v(11.28, -38.82) * mm});
            skLineSegment(sketch, "E31.11.16.0", {"start": v(7.84, -37.01) * mm, "end": v(7.38, -35.3) * mm});
            skPoint(sketch, "E31.14.16.0", {"position": v(7.25, -34.81) * mm});
            skPoint(sketch, "E31.15.16.0", {"position": v(11.78, -36.23) * mm});
            skArc(sketch, "E31.16.16.0", {"start": v(8.07, -37.5) * mm, "mid": v(8.8, -38.43) * mm, "end": v(9.64, -39.26) * mm});
            skPoint(sketch, "E31.17.16.0", {"position": v(7.91, -37.27) * mm});
            skArc(sketch, "E31.20.16.0", {"start": v(11.6, -33.62) * mm, "mid": v(11.3, -33.87) * mm, "end": v(11.25, -34.26) * mm});
            skArc(sketch, "E31.24.16.0", {"start": v(7.38, -35.3) * mm, "mid": v(7.15, -34.98) * mm, "end": v(6.77, -34.91) * mm});
            skArc(sketch, "E31.28.16.0", {"start": v(9.64, -39.26) * mm, "mid": v(9.85, -39.37) * mm, "end": v(10.1, -39.37) * mm});
            skArc(sketch, "E31.32.16.0", {"start": v(11.76, -36.52) * mm, "mid": v(11.76, -36.25) * mm, "end": v(11.71, -35.98) * mm});
            skLineSegment(sketch, "E31.36.16.0", {"start": v(10.1, -39.37) * mm, "end": v(10.52, -39.26) * mm});
            skArc(sketch, "E31.39.16.0", {"start": v(10.94, -39.14) * mm, "mid": v(11.15, -39.02) * mm, "end": v(11.28, -38.82) * mm});
            skLineSegment(sketch, "E31.43.16.0", {"start": v(10.94, -39.14) * mm, "end": v(10.52, -39.26) * mm});
            skArc(sketch, "E31.46.16.0", {"start": v(7.84, -37.01) * mm, "mid": v(7.94, -37.27) * mm, "end": v(8.07, -37.5) * mm});
            skPoint(sketch, "E31.1.17.0", {"position": v(17.9, -30.72) * mm});
            skLineSegment(sketch, "E31.2.17.0", {"start": v(18.94, -32.76) * mm, "end": v(18.13, -31.17) * mm});
            skPoint(sketch, "E31.5.17.0", {"position": v(19.07, -35.89) * mm});
            skPoint(sketch, "E31.6.17.0", {"position": v(17.83, -36.52) * mm});
            skArc(sketch, "E31.7.17.0", {"start": v(19.1, -33.28) * mm, "mid": v(19.17, -34.45) * mm, "end": v(19.1, -35.62) * mm});
            skLineSegment(sketch, "E31.11.17.0", {"start": v(15.37, -34.57) * mm, "end": v(14.56, -32.99) * mm});
            skPoint(sketch, "E31.14.17.0", {"position": v(14.33, -32.54) * mm});
            skPoint(sketch, "E31.15.17.0", {"position": v(19.06, -33) * mm});
            skArc(sketch, "E31.16.17.0", {"start": v(15.7, -35.01) * mm, "mid": v(16.6, -35.76) * mm, "end": v(17.6, -36.4) * mm});
            skPoint(sketch, "E31.17.17.0", {"position": v(15.49, -34.8) * mm});
            skArc(sketch, "E31.20.17.0", {"start": v(18.33, -30.47) * mm, "mid": v(18.1, -30.78) * mm, "end": v(18.13, -31.17) * mm});
            skArc(sketch, "E31.24.17.0", {"start": v(14.56, -32.99) * mm, "mid": v(14.27, -32.73) * mm, "end": v(13.88, -32.74) * mm});
            skArc(sketch, "E31.28.17.0", {"start": v(17.6, -36.4) * mm, "mid": v(17.82, -36.46) * mm, "end": v(18.06, -36.4) * mm});
            skArc(sketch, "E31.32.17.0", {"start": v(19.1, -33.28) * mm, "mid": v(19.04, -33) * mm, "end": v(18.94, -32.76) * mm});
            skLineSegment(sketch, "E31.36.17.0", {"start": v(18.06, -36.4) * mm, "end": v(18.45, -36.22) * mm});
            skArc(sketch, "E31.39.17.0", {"start": v(18.84, -36.01) * mm, "mid": v(19.02, -35.85) * mm, "end": v(19.1, -35.62) * mm});
            skLineSegment(sketch, "E31.43.17.0", {"start": v(18.84, -36.01) * mm, "end": v(18.45, -36.22) * mm});
            skArc(sketch, "E31.46.17.0", {"start": v(15.37, -34.57) * mm, "mid": v(15.51, -34.8) * mm, "end": v(15.7, -35.01) * mm});
            skPoint(sketch, "E31.1.18.0", {"position": v(23.9, -26.33) * mm});
            skLineSegment(sketch, "E31.2.18.0", {"start": v(25.33, -28.1) * mm, "end": v(24.21, -26.72) * mm});
            skPoint(sketch, "E31.5.18.0", {"position": v(26.11, -31.14) * mm});
            skPoint(sketch, "E31.6.18.0", {"position": v(25.03, -32.02) * mm});
            skArc(sketch, "E31.7.18.0", {"start": v(25.6, -28.58) * mm, "mid": v(25.92, -29.71) * mm, "end": v(26.1, -30.87) * mm});
            skLineSegment(sketch, "E31.11.18.0", {"start": v(22.22, -30.62) * mm, "end": v(21.1, -29.24) * mm});
            skPoint(sketch, "E31.14.18.0", {"position": v(20.79, -28.85) * mm});
            skPoint(sketch, "E31.15.18.0", {"position": v(25.5, -28.3) * mm});
            skArc(sketch, "E31.16.18.0", {"start": v(22.63, -30.98) * mm, "mid": v(23.67, -31.53) * mm, "end": v(24.77, -31.94) * mm});
            skPoint(sketch, "E31.17.18.0", {"position": v(22.39, -30.83) * mm});
            skArc(sketch, "E31.20.18.0", {"start": v(24.27, -26) * mm, "mid": v(24.1, -26.35) * mm, "end": v(24.21, -26.72) * mm});
            skArc(sketch, "E31.24.18.0", {"start": v(21.1, -29.24) * mm, "mid": v(20.76, -29.05) * mm, "end": v(20.38, -29.14) * mm});
            skArc(sketch, "E31.28.18.0", {"start": v(24.77, -31.94) * mm, "mid": v(25.01, -31.96) * mm, "end": v(25.23, -31.86) * mm});
            skArc(sketch, "E31.32.18.0", {"start": v(25.6, -28.58) * mm, "mid": v(25.49, -28.33) * mm, "end": v(25.33, -28.1) * mm});
            skLineSegment(sketch, "E31.36.18.0", {"start": v(25.23, -31.86) * mm, "end": v(25.58, -31.59) * mm});
            skArc(sketch, "E31.39.18.0", {"start": v(25.91, -31.3) * mm, "mid": v(26.06, -31.11) * mm, "end": v(26.1, -30.87) * mm});
            skLineSegment(sketch, "E31.43.18.0", {"start": v(25.91, -31.3) * mm, "end": v(25.58, -31.59) * mm});
            skArc(sketch, "E31.46.18.0", {"start": v(22.22, -30.62) * mm, "mid": v(22.41, -30.82) * mm, "end": v(22.63, -30.98) * mm});
            skPoint(sketch, "E31.1.19.0", {"position": v(28.85, -20.79) * mm});
            skLineSegment(sketch, "E31.2.19.0", {"start": v(30.62, -22.22) * mm, "end": v(29.24, -21.1) * mm});
            skPoint(sketch, "E31.5.19.0", {"position": v(32.02, -25.03) * mm});
            skPoint(sketch, "E31.6.19.0", {"position": v(31.14, -26.11) * mm});
            skArc(sketch, "E31.7.19.0", {"start": v(30.98, -22.63) * mm, "mid": v(31.53, -23.67) * mm, "end": v(31.94, -24.77) * mm});
            skLineSegment(sketch, "E31.11.19.0", {"start": v(28.1, -25.33) * mm, "end": v(26.72, -24.21) * mm});
            skPoint(sketch, "E31.14.19.0", {"position": v(26.33, -23.9) * mm});
            skPoint(sketch, "E31.15.19.0", {"position": v(30.83, -22.39) * mm});
            skArc(sketch, "E31.16.19.0", {"start": v(28.58, -25.6) * mm, "mid": v(29.71, -25.92) * mm, "end": v(30.87, -26.1) * mm});
            skPoint(sketch, "E31.17.19.0", {"position": v(28.3, -25.5) * mm});
            skArc(sketch, "E31.20.19.0", {"start": v(29.14, -20.38) * mm, "mid": v(29.05, -20.76) * mm, "end": v(29.24, -21.1) * mm});
            skArc(sketch, "E31.24.19.0", {"start": v(26.72, -24.21) * mm, "mid": v(26.35, -24.1) * mm, "end": v(26, -24.27) * mm});
            skArc(sketch, "E31.28.19.0", {"start": v(30.87, -26.1) * mm, "mid": v(31.11, -26.06) * mm, "end": v(31.3, -25.91) * mm});
            skArc(sketch, "E31.32.19.0", {"start": v(30.98, -22.63) * mm, "mid": v(30.82, -22.41) * mm, "end": v(30.62, -22.22) * mm});
            skLineSegment(sketch, "E31.36.19.0", {"start": v(31.3, -25.91) * mm, "end": v(31.59, -25.58) * mm});
            skArc(sketch, "E31.39.19.0", {"start": v(31.86, -25.23) * mm, "mid": v(31.96, -25.01) * mm, "end": v(31.94, -24.77) * mm});
            skLineSegment(sketch, "E31.43.19.0", {"start": v(31.86, -25.23) * mm, "end": v(31.59, -25.58) * mm});
            skArc(sketch, "E31.46.19.0", {"start": v(28.1, -25.33) * mm, "mid": v(28.33, -25.49) * mm, "end": v(28.58, -25.6) * mm});
            skPoint(sketch, "E31.1.20.0", {"position": v(32.54, -14.33) * mm});
            skLineSegment(sketch, "E31.2.20.0", {"start": v(34.57, -15.37) * mm, "end": v(32.99, -14.56) * mm});
            skPoint(sketch, "E31.5.20.0", {"position": v(36.52, -17.83) * mm});
            skPoint(sketch, "E31.6.20.0", {"position": v(35.89, -19.07) * mm});
            skArc(sketch, "E31.7.20.0", {"start": v(35.01, -15.7) * mm, "mid": v(35.76, -16.6) * mm, "end": v(36.4, -17.6) * mm});
            skLineSegment(sketch, "E31.11.20.0", {"start": v(32.76, -18.94) * mm, "end": v(31.17, -18.13) * mm});
            skPoint(sketch, "E31.14.20.0", {"position": v(30.72, -17.9) * mm});
            skPoint(sketch, "E31.15.20.0", {"position": v(34.8, -15.49) * mm});
            skArc(sketch, "E31.16.20.0", {"start": v(33.28, -19.1) * mm, "mid": v(34.45, -19.17) * mm, "end": v(35.62, -19.1) * mm});
            skPoint(sketch, "E31.17.20.0", {"position": v(33, -19.06) * mm});
            skArc(sketch, "E31.20.20.0", {"start": v(32.74, -13.88) * mm, "mid": v(32.73, -14.27) * mm, "end": v(32.99, -14.56) * mm});
            skArc(sketch, "E31.24.20.0", {"start": v(31.17, -18.13) * mm, "mid": v(30.78, -18.1) * mm, "end": v(30.47, -18.33) * mm});
            skArc(sketch, "E31.28.20.0", {"start": v(35.62, -19.1) * mm, "mid": v(35.85, -19.02) * mm, "end": v(36.01, -18.84) * mm});
            skArc(sketch, "E31.32.20.0", {"start": v(35.01, -15.7) * mm, "mid": v(34.8, -15.51) * mm, "end": v(34.57, -15.37) * mm});
            skLineSegment(sketch, "E31.36.20.0", {"start": v(36.01, -18.84) * mm, "end": v(36.22, -18.45) * mm});
            skArc(sketch, "E31.39.20.0", {"start": v(36.4, -18.06) * mm, "mid": v(36.46, -17.82) * mm, "end": v(36.4, -17.6) * mm});
            skLineSegment(sketch, "E31.43.20.0", {"start": v(36.4, -18.06) * mm, "end": v(36.22, -18.45) * mm});
            skArc(sketch, "E31.46.20.0", {"start": v(32.76, -18.94) * mm, "mid": v(33, -19.04) * mm, "end": v(33.28, -19.1) * mm});
            skPoint(sketch, "E31.1.21.0", {"position": v(34.81, -7.25) * mm});
            skLineSegment(sketch, "E31.2.21.0", {"start": v(37.01, -7.84) * mm, "end": v(35.3, -7.38) * mm});
            skPoint(sketch, "E31.5.21.0", {"position": v(39.43, -9.84) * mm});
            skPoint(sketch, "E31.6.21.0", {"position": v(39.07, -11.2) * mm});
            skArc(sketch, "E31.7.21.0", {"start": v(37.5, -8.07) * mm, "mid": v(38.43, -8.8) * mm, "end": v(39.26, -9.64) * mm});
            skLineSegment(sketch, "E31.11.21.0", {"start": v(35.98, -11.71) * mm, "end": v(34.26, -11.25) * mm});
            skPoint(sketch, "E31.14.21.0", {"position": v(33.78, -11.12) * mm});
            skPoint(sketch, "E31.15.21.0", {"position": v(37.27, -7.91) * mm});
            skArc(sketch, "E31.16.21.0", {"start": v(36.52, -11.76) * mm, "mid": v(37.68, -11.6) * mm, "end": v(38.82, -11.28) * mm});
            skPoint(sketch, "E31.17.21.0", {"position": v(36.23, -11.78) * mm});
            skArc(sketch, "E31.20.21.0", {"start": v(34.91, -6.77) * mm, "mid": v(34.98, -7.15) * mm, "end": v(35.3, -7.38) * mm});
            skArc(sketch, "E31.24.21.0", {"start": v(34.26, -11.25) * mm, "mid": v(33.87, -11.3) * mm, "end": v(33.62, -11.6) * mm});
            skArc(sketch, "E31.28.21.0", {"start": v(38.82, -11.28) * mm, "mid": v(39.02, -11.15) * mm, "end": v(39.14, -10.94) * mm});
            skArc(sketch, "E31.32.21.0", {"start": v(37.5, -8.07) * mm, "mid": v(37.27, -7.94) * mm, "end": v(37.01, -7.84) * mm});
            skLineSegment(sketch, "E31.36.21.0", {"start": v(39.14, -10.94) * mm, "end": v(39.26, -10.52) * mm});
            skArc(sketch, "E31.39.21.0", {"start": v(39.37, -10.1) * mm, "mid": v(39.37, -9.85) * mm, "end": v(39.26, -9.64) * mm});
            skLineSegment(sketch, "E31.43.21.0", {"start": v(39.37, -10.1) * mm, "end": v(39.26, -10.52) * mm});
            skArc(sketch, "E31.46.21.0", {"start": v(35.98, -11.71) * mm, "mid": v(36.25, -11.76) * mm, "end": v(36.52, -11.76) * mm});
            skPoint(sketch, "E31.1.22.0", {"position": v(35.56, 0.14) * mm});
            skLineSegment(sketch, "E31.2.22.0", {"start": v(37.84, 0.02) * mm, "end": v(36.06, 0.12) * mm});
            skPoint(sketch, "E31.5.22.0", {"position": v(40.61, -1.43) * mm});
            skPoint(sketch, "E31.6.22.0", {"position": v(40.54, -2.82) * mm});
            skArc(sketch, "E31.7.22.0", {"start": v(38.37, -0.1) * mm, "mid": v(39.42, -0.62) * mm, "end": v(40.4, -1.27) * mm});
            skLineSegment(sketch, "E31.11.22.0", {"start": v(37.63, -3.98) * mm, "end": v(35.85, -3.88) * mm});
            skPoint(sketch, "E31.14.22.0", {"position": v(35.35, -3.86) * mm});
            skPoint(sketch, "E31.15.22.0", {"position": v(38.1, 0) * mm});
            skArc(sketch, "E31.16.22.0", {"start": v(38.17, -3.91) * mm, "mid": v(39.27, -3.5) * mm, "end": v(40.31, -2.96) * mm});
            skPoint(sketch, "E31.17.22.0", {"position": v(37.9, -4) * mm});
            skArc(sketch, "E31.20.22.0", {"start": v(35.55, 0.64) * mm, "mid": v(35.7, 0.28) * mm, "end": v(36.06, 0.12) * mm});
            skArc(sketch, "E31.24.22.0", {"start": v(35.85, -3.88) * mm, "mid": v(35.48, -4) * mm, "end": v(35.3, -4.35) * mm});
            skArc(sketch, "E31.28.22.0", {"start": v(40.31, -2.96) * mm, "mid": v(40.49, -2.8) * mm, "end": v(40.56, -2.56) * mm});
            skArc(sketch, "E31.32.22.0", {"start": v(38.37, -0.1) * mm, "mid": v(38.1, -0.02) * mm, "end": v(37.84, 0.02) * mm});
            skLineSegment(sketch, "E31.36.22.0", {"start": v(40.56, -2.56) * mm, "end": v(40.6, -2.13) * mm});
            skArc(sketch, "E31.39.22.0", {"start": v(40.6, -1.7) * mm, "mid": v(40.56, -1.45) * mm, "end": v(40.4, -1.27) * mm});
            skLineSegment(sketch, "E31.43.22.0", {"start": v(40.6, -1.7) * mm, "end": v(40.6, -2.13) * mm});
            skArc(sketch, "E31.46.22.0", {"start": v(37.63, -3.98) * mm, "mid": v(37.9, -3.97) * mm, "end": v(38.17, -3.91) * mm});
            skPoint(sketch, "E31.1.23.0", {"position": v(34.75, 7.53) * mm});
            skLineSegment(sketch, "E31.2.23.0", {"start": v(37, 7.89) * mm, "end": v(35.25, 7.61) * mm});
            skPoint(sketch, "E31.5.23.0", {"position": v(40.02, 7.05) * mm});
            skPoint(sketch, "E31.6.23.0", {"position": v(40.24, 5.67) * mm});
            skArc(sketch, "E31.7.23.0", {"start": v(37.55, 7.88) * mm, "mid": v(38.69, 7.6) * mm, "end": v(39.78, 7.16) * mm});
            skLineSegment(sketch, "E31.11.23.0", {"start": v(37.63, 3.93) * mm, "end": v(35.87, 3.65) * mm});
            skPoint(sketch, "E31.14.23.0", {"position": v(35.38, 3.58) * mm});
            skPoint(sketch, "E31.15.23.0", {"position": v(37.27, 7.93) * mm});
            skArc(sketch, "E31.16.23.0", {"start": v(38.15, 4.1) * mm, "mid": v(39.14, 4.74) * mm, "end": v(40.05, 5.48) * mm});
            skPoint(sketch, "E31.17.23.0", {"position": v(37.9, 3.97) * mm});
            skArc(sketch, "E31.20.23.0", {"start": v(34.64, 8.02) * mm, "mid": v(34.87, 7.7) * mm, "end": v(35.25, 7.61) * mm});
            skArc(sketch, "E31.24.23.0", {"start": v(35.87, 3.65) * mm, "mid": v(35.54, 3.46) * mm, "end": v(35.43, 3.08) * mm});
            skArc(sketch, "E31.28.23.0", {"start": v(40.05, 5.48) * mm, "mid": v(40.18, 5.68) * mm, "end": v(40.2, 5.93) * mm});
            skArc(sketch, "E31.32.23.0", {"start": v(37.55, 7.88) * mm, "mid": v(37.28, 7.9) * mm, "end": v(37, 7.89) * mm});
            skLineSegment(sketch, "E31.36.23.0", {"start": v(40.2, 5.93) * mm, "end": v(40.15, 6.36) * mm});
            skArc(sketch, "E31.39.23.0", {"start": v(40.07, 6.79) * mm, "mid": v(39.97, 7.01) * mm, "end": v(39.78, 7.16) * mm});
            skLineSegment(sketch, "E31.43.23.0", {"start": v(40.07, 6.79) * mm, "end": v(40.15, 6.36) * mm});
            skArc(sketch, "E31.46.23.0", {"start": v(37.63, 3.93) * mm, "mid": v(37.9, 4) * mm, "end": v(38.15, 4.1) * mm});
            skPoint(sketch, "E31.1.24.0", {"position": v(32.43, 14.6) * mm});
            skLineSegment(sketch, "E31.2.24.0", {"start": v(34.56, 15.41) * mm, "end": v(32.9, 14.77) * mm});
            skPoint(sketch, "E31.5.24.0", {"position": v(37.69, 15.21) * mm});
            skPoint(sketch, "E31.6.24.0", {"position": v(38.19, 13.91) * mm});
            skArc(sketch, "E31.7.24.0", {"start": v(35.1, 15.52) * mm, "mid": v(36.27, 15.47) * mm, "end": v(37.43, 15.28) * mm});
            skLineSegment(sketch, "E31.11.24.0", {"start": v(36, 11.67) * mm, "end": v(34.33, 11.03) * mm});
            skPoint(sketch, "E31.14.24.0", {"position": v(33.86, 10.85) * mm});
            skPoint(sketch, "E31.15.24.0", {"position": v(34.8, 15.5) * mm});
            skArc(sketch, "E31.16.24.0", {"start": v(36.46, 11.95) * mm, "mid": v(37.3, 12.77) * mm, "end": v(38.03, 13.69) * mm});
            skPoint(sketch, "E31.17.24.0", {"position": v(36.24, 11.77) * mm});
            skArc(sketch, "E31.20.24.0", {"start": v(32.22, 15.04) * mm, "mid": v(32.5, 14.78) * mm, "end": v(32.9, 14.77) * mm});
            skArc(sketch, "E31.24.24.0", {"start": v(34.33, 11.03) * mm, "mid": v(34.04, 10.77) * mm, "end": v(34.01, 10.38) * mm});
            skArc(sketch, "E31.28.24.0", {"start": v(38.03, 13.69) * mm, "mid": v(38.12, 13.91) * mm, "end": v(38.1, 14.16) * mm});
            skArc(sketch, "E31.32.24.0", {"start": v(35.1, 15.52) * mm, "mid": v(34.82, 15.49) * mm, "end": v(34.56, 15.41) * mm});
            skLineSegment(sketch, "E31.36.24.0", {"start": v(38.1, 14.16) * mm, "end": v(37.95, 14.57) * mm});
            skArc(sketch, "E31.39.24.0", {"start": v(37.78, 14.97) * mm, "mid": v(37.64, 15.17) * mm, "end": v(37.43, 15.28) * mm});
            skLineSegment(sketch, "E31.43.24.0", {"start": v(37.78, 14.97) * mm, "end": v(37.95, 14.57) * mm});
            skArc(sketch, "E31.46.24.0", {"start": v(36, 11.67) * mm, "mid": v(36.24, 11.8) * mm, "end": v(36.46, 11.95) * mm});
            skPoint(sketch, "E31.1.25.0", {"position": v(28.69, 21.02) * mm});
            skLineSegment(sketch, "E31.2.25.0", {"start": v(30.6, 22.26) * mm, "end": v(29.1, 21.29) * mm});
            skPoint(sketch, "E31.5.25.0", {"position": v(33.7, 22.72) * mm});
            skPoint(sketch, "E31.6.25.0", {"position": v(34.46, 21.55) * mm});
            skArc(sketch, "E31.7.25.0", {"start": v(31.1, 22.47) * mm, "mid": v(32.26, 22.67) * mm, "end": v(33.43, 22.72) * mm});
            skLineSegment(sketch, "E31.11.25.0", {"start": v(32.78, 18.9) * mm, "end": v(31.29, 17.93) * mm});
            skPoint(sketch, "E31.14.25.0", {"position": v(30.87, 17.66) * mm});
            skPoint(sketch, "E31.15.25.0", {"position": v(30.82, 22.4) * mm});
            skArc(sketch, "E31.16.25.0", {"start": v(33.18, 19.27) * mm, "mid": v(33.83, 20.25) * mm, "end": v(34.36, 21.3) * mm});
            skPoint(sketch, "E31.17.25.0", {"position": v(33, 19.04) * mm});
            skArc(sketch, "E31.20.25.0", {"start": v(28.39, 21.41) * mm, "mid": v(28.72, 21.21) * mm, "end": v(29.1, 21.29) * mm});
            skArc(sketch, "E31.24.25.0", {"start": v(31.29, 17.93) * mm, "mid": v(31.06, 17.61) * mm, "end": v(31.11, 17.22) * mm});
            skArc(sketch, "E31.28.25.0", {"start": v(34.36, 21.3) * mm, "mid": v(34.4, 21.54) * mm, "end": v(34.32, 21.77) * mm});
            skArc(sketch, "E31.32.25.0", {"start": v(31.1, 22.47) * mm, "mid": v(30.84, 22.39) * mm, "end": v(30.6, 22.26) * mm});
            skLineSegment(sketch, "E31.36.25.0", {"start": v(34.32, 21.77) * mm, "end": v(34.09, 22.14) * mm});
            skArc(sketch, "E31.39.25.0", {"start": v(33.84, 22.5) * mm, "mid": v(33.67, 22.66) * mm, "end": v(33.43, 22.72) * mm});
            skLineSegment(sketch, "E31.43.25.0", {"start": v(33.84, 22.5) * mm, "end": v(34.09, 22.14) * mm});
            skArc(sketch, "E31.46.25.0", {"start": v(32.78, 18.9) * mm, "mid": v(33, 19.07) * mm, "end": v(33.18, 19.27) * mm});
            skPoint(sketch, "E31.1.26.0", {"position": v(23.69, 26.52) * mm});
            skLineSegment(sketch, "E31.2.26.0", {"start": v(25.3, 28.13) * mm, "end": v(24.04, 26.87) * mm});
            skPoint(sketch, "E31.5.26.0", {"position": v(28.24, 29.23) * mm});
            skPoint(sketch, "E31.6.26.0", {"position": v(29.23, 28.24) * mm});
            skArc(sketch, "E31.7.26.0", {"start": v(25.75, 28.45) * mm, "mid": v(26.84, 28.88) * mm, "end": v(27.98, 29.18) * mm});
            skLineSegment(sketch, "E31.11.26.0", {"start": v(28.13, 25.3) * mm, "end": v(26.87, 24.04) * mm});
            skPoint(sketch, "E31.14.26.0", {"position": v(26.52, 23.69) * mm});
            skPoint(sketch, "E31.15.26.0", {"position": v(25.49, 28.32) * mm});
            skArc(sketch, "E31.16.26.0", {"start": v(28.45, 25.75) * mm, "mid": v(28.88, 26.84) * mm, "end": v(29.18, 27.98) * mm});
            skPoint(sketch, "E31.17.26.0", {"position": v(28.32, 25.49) * mm});
            skArc(sketch, "E31.20.26.0", {"start": v(23.32, 26.85) * mm, "mid": v(23.68, 26.72) * mm, "end": v(24.04, 26.87) * mm});
            skArc(sketch, "E31.24.26.0", {"start": v(26.87, 24.04) * mm, "mid": v(26.72, 23.68) * mm, "end": v(26.85, 23.32) * mm});
            skArc(sketch, "E31.28.26.0", {"start": v(29.18, 27.98) * mm, "mid": v(29.17, 28.22) * mm, "end": v(29.04, 28.43) * mm});
            skArc(sketch, "E31.32.26.0", {"start": v(25.75, 28.45) * mm, "mid": v(25.51, 28.3) * mm, "end": v(25.3, 28.13) * mm});
            skLineSegment(sketch, "E31.36.26.0", {"start": v(29.04, 28.43) * mm, "end": v(28.74, 28.74) * mm});
            skArc(sketch, "E31.39.26.0", {"start": v(28.43, 29.04) * mm, "mid": v(28.22, 29.17) * mm, "end": v(27.98, 29.18) * mm});
            skLineSegment(sketch, "E31.43.26.0", {"start": v(28.43, 29.04) * mm, "end": v(28.74, 28.74) * mm});
            skArc(sketch, "E31.46.26.0", {"start": v(28.13, 25.3) * mm, "mid": v(28.3, 25.51) * mm, "end": v(28.45, 25.75) * mm});
            skPoint(sketch, "E31.1.27.0", {"position": v(17.66, 30.87) * mm});
            skLineSegment(sketch, "E31.2.27.0", {"start": v(18.9, 32.78) * mm, "end": v(17.93, 31.29) * mm});
            skPoint(sketch, "E31.5.27.0", {"position": v(21.55, 34.46) * mm});
            skPoint(sketch, "E31.6.27.0", {"position": v(22.72, 33.7) * mm});
            skArc(sketch, "E31.7.27.0", {"start": v(19.27, 33.18) * mm, "mid": v(20.25, 33.83) * mm, "end": v(21.3, 34.36) * mm});
            skLineSegment(sketch, "E31.11.27.0", {"start": v(22.26, 30.6) * mm, "end": v(21.29, 29.1) * mm});
            skPoint(sketch, "E31.14.27.0", {"position": v(21.02, 28.69) * mm});
            skPoint(sketch, "E31.15.27.0", {"position": v(19.04, 33) * mm});
            skArc(sketch, "E31.16.27.0", {"start": v(22.47, 31.1) * mm, "mid": v(22.67, 32.26) * mm, "end": v(22.72, 33.43) * mm});
            skPoint(sketch, "E31.17.27.0", {"position": v(22.4, 30.82) * mm});
            skArc(sketch, "E31.20.27.0", {"start": v(17.22, 31.11) * mm, "mid": v(17.61, 31.06) * mm, "end": v(17.93, 31.29) * mm});
            skArc(sketch, "E31.24.27.0", {"start": v(21.29, 29.1) * mm, "mid": v(21.21, 28.72) * mm, "end": v(21.41, 28.39) * mm});
            skArc(sketch, "E31.28.27.0", {"start": v(22.72, 33.43) * mm, "mid": v(22.66, 33.67) * mm, "end": v(22.5, 33.84) * mm});
            skArc(sketch, "E31.32.27.0", {"start": v(19.27, 33.18) * mm, "mid": v(19.07, 33) * mm, "end": v(18.9, 32.78) * mm});
            skLineSegment(sketch, "E31.36.27.0", {"start": v(22.5, 33.84) * mm, "end": v(22.14, 34.09) * mm});
            skArc(sketch, "E31.39.27.0", {"start": v(21.77, 34.32) * mm, "mid": v(21.54, 34.4) * mm, "end": v(21.3, 34.36) * mm});
            skLineSegment(sketch, "E31.43.27.0", {"start": v(21.77, 34.32) * mm, "end": v(22.14, 34.09) * mm});
            skArc(sketch, "E31.46.27.0", {"start": v(22.26, 30.6) * mm, "mid": v(22.39, 30.84) * mm, "end": v(22.47, 31.1) * mm});
            skPoint(sketch, "E31.1.28.0", {"position": v(10.85, 33.86) * mm});
            skLineSegment(sketch, "E31.2.28.0", {"start": v(11.67, 36) * mm, "end": v(11.03, 34.33) * mm});
            skPoint(sketch, "E31.5.28.0", {"position": v(13.91, 38.19) * mm});
            skPoint(sketch, "E31.6.28.0", {"position": v(15.21, 37.69) * mm});
            skArc(sketch, "E31.7.28.0", {"start": v(11.95, 36.46) * mm, "mid": v(12.77, 37.3) * mm, "end": v(13.69, 38.03) * mm});
            skLineSegment(sketch, "E31.11.28.0", {"start": v(15.41, 34.56) * mm, "end": v(14.77, 32.9) * mm});
            skPoint(sketch, "E31.14.28.0", {"position": v(14.6, 32.43) * mm});
            skPoint(sketch, "E31.15.28.0", {"position": v(11.77, 36.24) * mm});
            skArc(sketch, "E31.16.28.0", {"start": v(15.52, 35.1) * mm, "mid": v(15.47, 36.27) * mm, "end": v(15.28, 37.43) * mm});
            skPoint(sketch, "E31.17.28.0", {"position": v(15.5, 34.8) * mm});
            skArc(sketch, "E31.20.28.0", {"start": v(10.38, 34.01) * mm, "mid": v(10.77, 34.04) * mm, "end": v(11.03, 34.33) * mm});
            skArc(sketch, "E31.24.28.0", {"start": v(14.77, 32.9) * mm, "mid": v(14.78, 32.5) * mm, "end": v(15.04, 32.22) * mm});
            skArc(sketch, "E31.28.28.0", {"start": v(15.28, 37.43) * mm, "mid": v(15.17, 37.64) * mm, "end": v(14.97, 37.78) * mm});
            skArc(sketch, "E31.32.28.0", {"start": v(11.95, 36.46) * mm, "mid": v(11.8, 36.24) * mm, "end": v(11.67, 36) * mm});
            skLineSegment(sketch, "E31.36.28.0", {"start": v(14.97, 37.78) * mm, "end": v(14.57, 37.95) * mm});
            skArc(sketch, "E31.39.28.0", {"start": v(14.16, 38.1) * mm, "mid": v(13.91, 38.12) * mm, "end": v(13.69, 38.03) * mm});
            skLineSegment(sketch, "E31.43.28.0", {"start": v(14.16, 38.1) * mm, "end": v(14.57, 37.95) * mm});
            skArc(sketch, "E31.46.28.0", {"start": v(15.41, 34.56) * mm, "mid": v(15.49, 34.82) * mm, "end": v(15.52, 35.1) * mm});
            skPoint(sketch, "E31.1.29.0", {"position": v(3.58, 35.38) * mm});
            skLineSegment(sketch, "E31.2.29.0", {"start": v(3.93, 37.63) * mm, "end": v(3.65, 35.87) * mm});
            skPoint(sketch, "E31.5.29.0", {"position": v(5.67, 40.24) * mm});
            skPoint(sketch, "E31.6.29.0", {"position": v(7.05, 40.02) * mm});
            skArc(sketch, "E31.7.29.0", {"start": v(4.1, 38.15) * mm, "mid": v(4.74, 39.14) * mm, "end": v(5.48, 40.05) * mm});
            skLineSegment(sketch, "E31.11.29.0", {"start": v(7.89, 37) * mm, "end": v(7.61, 35.25) * mm});
            skPoint(sketch, "E31.14.29.0", {"position": v(7.53, 34.75) * mm});
            skPoint(sketch, "E31.15.29.0", {"position": v(3.97, 37.9) * mm});
            skArc(sketch, "E31.16.29.0", {"start": v(7.88, 37.55) * mm, "mid": v(7.6, 38.69) * mm, "end": v(7.16, 39.78) * mm});
            skPoint(sketch, "E31.17.29.0", {"position": v(7.93, 37.27) * mm});
            skArc(sketch, "E31.20.29.0", {"start": v(3.08, 35.43) * mm, "mid": v(3.46, 35.54) * mm, "end": v(3.65, 35.87) * mm});
            skArc(sketch, "E31.24.29.0", {"start": v(7.61, 35.25) * mm, "mid": v(7.7, 34.87) * mm, "end": v(8.02, 34.64) * mm});
            skArc(sketch, "E31.28.29.0", {"start": v(7.16, 39.78) * mm, "mid": v(7.01, 39.97) * mm, "end": v(6.79, 40.07) * mm});
            skArc(sketch, "E31.32.29.0", {"start": v(4.1, 38.15) * mm, "mid": v(4, 37.9) * mm, "end": v(3.93, 37.63) * mm});
            skLineSegment(sketch, "E31.36.29.0", {"start": v(6.79, 40.07) * mm, "end": v(6.36, 40.15) * mm});
            skArc(sketch, "E31.39.29.0", {"start": v(5.93, 40.2) * mm, "mid": v(5.68, 40.18) * mm, "end": v(5.48, 40.05) * mm});
            skLineSegment(sketch, "E31.43.29.0", {"start": v(5.93, 40.2) * mm, "end": v(6.36, 40.15) * mm});
            skArc(sketch, "E31.46.29.0", {"start": v(7.89, 37) * mm, "mid": v(7.9, 37.28) * mm, "end": v(7.88, 37.55) * mm});
            skLineSegment(sketch, "E32", {"start": v(0.64, 35.55) * mm, "end": v(3.08, 35.43) * mm});
            skLineSegment(sketch, "E33.1.0", {"start": v(-6.77, 34.91) * mm, "end": v(-4.35, 35.3) * mm});
            skLineSegment(sketch, "E33.2.0", {"start": v(-13.88, 32.74) * mm, "end": v(-11.6, 33.62) * mm});
            skLineSegment(sketch, "E33.3.0", {"start": v(-20.38, 29.14) * mm, "end": v(-18.33, 30.47) * mm});
            skLineSegment(sketch, "E33.4.0", {"start": v(-26, 24.27) * mm, "end": v(-24.27, 26) * mm});
            skLineSegment(sketch, "E33.5.0", {"start": v(-30.47, 18.33) * mm, "end": v(-29.14, 20.38) * mm});
            skLineSegment(sketch, "E33.6.0", {"start": v(-33.62, 11.6) * mm, "end": v(-32.74, 13.88) * mm});
            skLineSegment(sketch, "E33.7.0", {"start": v(-35.3, 4.35) * mm, "end": v(-34.91, 6.77) * mm});
            skLineSegment(sketch, "E33.8.0", {"start": v(-35.43, -3.08) * mm, "end": v(-35.55, -0.64) * mm});
            skLineSegment(sketch, "E33.9.0", {"start": v(-34.01, -10.38) * mm, "end": v(-34.64, -8.02) * mm});
            skLineSegment(sketch, "E33.10.0", {"start": v(-31.11, -17.22) * mm, "end": v(-32.22, -15.04) * mm});
            skLineSegment(sketch, "E33.11.0", {"start": v(-26.85, -23.32) * mm, "end": v(-28.39, -21.41) * mm});
            skLineSegment(sketch, "E33.12.0", {"start": v(-21.41, -28.39) * mm, "end": v(-23.32, -26.85) * mm});
            skLineSegment(sketch, "E33.13.0", {"start": v(-15.04, -32.22) * mm, "end": v(-17.22, -31.11) * mm});
            skLineSegment(sketch, "E33.14.0", {"start": v(-8.02, -34.64) * mm, "end": v(-10.38, -34.01) * mm});
            skLineSegment(sketch, "E33.15.0", {"start": v(-0.64, -35.55) * mm, "end": v(-3.08, -35.43) * mm});
            skLineSegment(sketch, "E33.16.0", {"start": v(6.77, -34.91) * mm, "end": v(4.35, -35.3) * mm});
            skLineSegment(sketch, "E33.17.0", {"start": v(13.88, -32.74) * mm, "end": v(11.6, -33.62) * mm});
            skLineSegment(sketch, "E33.18.0", {"start": v(20.38, -29.14) * mm, "end": v(18.33, -30.47) * mm});
            skLineSegment(sketch, "E33.19.0", {"start": v(26, -24.27) * mm, "end": v(24.27, -26) * mm});
            skLineSegment(sketch, "E33.20.0", {"start": v(30.47, -18.33) * mm, "end": v(29.14, -20.38) * mm});
            skLineSegment(sketch, "E33.21.0", {"start": v(33.62, -11.6) * mm, "end": v(32.74, -13.88) * mm});
            skLineSegment(sketch, "E33.22.0", {"start": v(35.3, -4.35) * mm, "end": v(34.91, -6.77) * mm});
            skLineSegment(sketch, "E33.23.0", {"start": v(35.43, 3.08) * mm, "end": v(35.55, 0.64) * mm});
            skLineSegment(sketch, "E33.24.0", {"start": v(34.01, 10.38) * mm, "end": v(34.64, 8.02) * mm});
            skLineSegment(sketch, "E33.25.0", {"start": v(31.11, 17.22) * mm, "end": v(32.22, 15.04) * mm});
            skLineSegment(sketch, "E33.26.0", {"start": v(26.85, 23.32) * mm, "end": v(28.39, 21.41) * mm});
            skLineSegment(sketch, "E33.27.0", {"start": v(21.41, 28.39) * mm, "end": v(23.32, 26.85) * mm});
            skLineSegment(sketch, "E33.28.0", {"start": v(15.04, 32.22) * mm, "end": v(17.22, 31.11) * mm});
            skLineSegment(sketch, "E33.29.0", {"start": v(8.02, 34.64) * mm, "end": v(10.38, 34.01) * mm});
            skSolve(sketch);
        }
        {
            var Q0;
            Q0=makeQuery(id+"F2.imprint","IMPRINT",FACE,{"disambiguationData":[TD([[makeQuery(id+"F2.imprint","IMPRINT",EDGE,{"derivedFrom":sQuery(id+"F2.wireOp",EDGE,"E18.trimOffspring")}),1.0]])]});
            var Q1;
            Q1=makeQuery(id+"F0.imprint","IMPRINT",FACE,{"disambiguationData":[TD([[makeQuery(id+"F0.imprint","IMPRINT",EDGE,{"derivedFrom":sQuery(id+"F0.wireOp",EDGE,"E0.trimOffspring")}),1.0]])]});
            var Q2;
            Q2=sQuery(id+"F0.wireOp",VERTEX,"E15.40.29.0.start");
            var Q3;
            Q3=sQuery(id+"F2.wireOp",VERTEX,"E30.1.12.start");
            loft(context, id + "F3", {"sheetProfilesArray" : [{ "sheetProfileEntities" : qUnion([Q0]) }, { "sheetProfileEntities" : qUnion([Q1]) }], "matchConnections" : true, "connections" : [{ "connectionEntities" : qUnion([Q2, Q3]), "connectionEdgeQueries" : qUnion([]), "connectionEdgeParameters" : [] }]});
        }
        {
            var Q0;
            Q0=makeQuery(id+"F3.opLoft","CAP_FACE",FACE,{"disambiguationData":[OSD([makeQuery(id+"F2.imprint","IMPRINT",FACE,{"disambiguationData":[TD([[makeQuery(id+"F2.imprint","IMPRINT",EDGE,{"derivedFrom":sQuery(id+"F2.wireOp",EDGE,"E18.trimOffspring")}),1.0]])]})])],"isStart":true});
            var sketch = newSketch(context, id + "F4", { "sketchPlane" : qUnion([Q0])});
            skCircle(sketch, "E34", {"center": v(0, 0) * mm, "radius": 6.35 * mm});
            skSolve(sketch);
        }
        {
            var Q0;
            Q0 = qSketchRegion(id + "F4", true);
            extrude(context, id + "F5", {"entities" : qUnion([Q0]), "operationType" : NewBodyOperationType.REMOVE, "oppositeDirection" : true, "depth" : 76.2 * mm});
        }
    });
